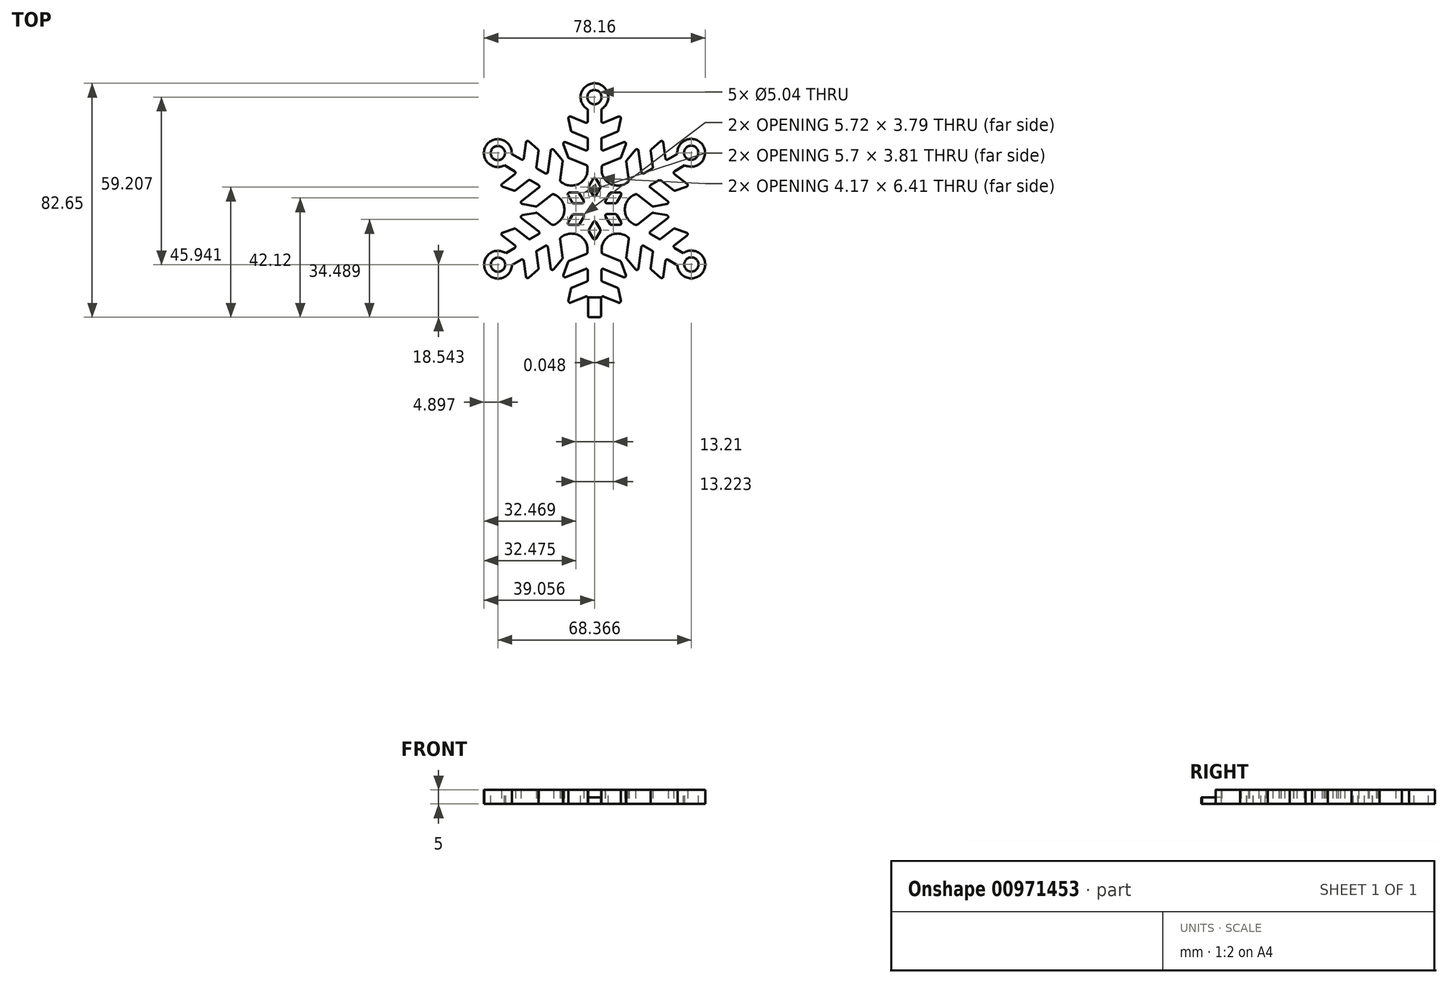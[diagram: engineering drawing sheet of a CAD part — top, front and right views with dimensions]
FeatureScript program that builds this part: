
annotation { "Feature Type Name" : "Feature", "Feature Type Description" : "" }
export const myFeature = defineFeature(function(context is Context, id is Id, definition is map)
    precondition{}
    {
        {
            var Q0;
            Q0=qCreatedBy(makeId("Top.planeOp"),FACE);
            var sketch = newSketch(context, id + "F0", { "sketchPlane" : qUnion([Q0])});
            skCircle(sketch, "E0", {"center": v(-1.7, 0) * mm, "radius": 57.15 * mm});
            skSolve(sketch);
        }
        {
            var Q0;
            Q0=makeQuery(id+"F0.imprint","IMPRINT",FACE,{"disambiguationData":[TD([[makeQuery(id+"F0.imprint","IMPRINT",EDGE,{"derivedFrom":sQuery(id+"F0.wireOp",EDGE,"E0")}),1.0]])]});
            extrude(context, id + "F1", {"entities" : qUnion([Q0]), "offsetDistance" : 25 * mm, "depth" : 6 * mm});
        }
        {
            var Q0;
            Q0=makeQuery(id+"F1.opExtrude","CAP_FACE",FACE,{"disambiguationData":[OSD([sQuery(id+"F0.wireOp",EDGE,"E0")])],"isStart":false});
            var sketch = newSketch(context, id + "F2", { "sketchPlane" : qUnion([Q0])});
            skCircle(sketch, "E1", {"center": v(0, 0) * mm, "radius": 19.2 * mm, "construction": true});
            skLineSegment(sketch, "E2", {"start": v(-23.76, 13.72) * mm, "end": v(23.98, -13.85) * mm, "construction": true});
            skLineSegment(sketch, "E3", {"start": v(-14.54, -25.2) * mm, "end": v(14.87, 25.76) * mm, "construction": true});
            skLineSegment(sketch, "E4", {"start": v(-12.51, -6.43) * mm, "end": v(-10.56, -3.05) * mm});
            skLineSegment(sketch, "E5", {"start": v(-9.89, -2.65) * mm, "end": v(-5.8, -2.57) * mm});
            skLineSegment(sketch, "E6", {"start": v(-5.1, -3.76) * mm, "end": v(-7.1, -7.22) * mm});
            skLineSegment(sketch, "E7", {"start": v(-7.8, -7.62) * mm, "end": v(-11.82, -7.62) * mm});
            skLineSegment(sketch, "E8", {"start": v(-13.2, -7.62) * mm, "end": v(-4.4, -2.54) * mm, "construction": true});
            skLineSegment(sketch, "E9", {"start": v(-10.33, -2.66) * mm, "end": v(-7.33, -7.62) * mm, "construction": true});
            skLineSegment(sketch, "E10", {"start": v(0, 0) * mm, "end": v(-16.62, -9.6) * mm, "construction": true});
            skPoint(sketch, "E11.visualSharp", {"position": v(-10.33, -2.66) * mm});
            skArc(sketch, "E11.filletArc", {"start": v(-9.89, -2.65) * mm, "mid": v(-10.27, -2.76) * mm, "end": v(-10.56, -3.05) * mm});
            skPoint(sketch, "E12.visualSharp", {"position": v(-7.33, -7.62) * mm});
            skArc(sketch, "E12.filletArc", {"start": v(-7.8, -7.62) * mm, "mid": v(-7.4, -7.51) * mm, "end": v(-7.1, -7.22) * mm});
            skPoint(sketch, "E13.visualSharp", {"position": v(-4.4, -2.54) * mm});
            skArc(sketch, "E13.filletArc", {"start": v(-5.1, -3.76) * mm, "mid": v(-5.1, -2.96) * mm, "end": v(-5.8, -2.57) * mm});
            skPoint(sketch, "E14.visualSharp", {"position": v(-13.2, -7.62) * mm});
            skArc(sketch, "E14.filletArc", {"start": v(-12.51, -6.43) * mm, "mid": v(-12.51, -7.22) * mm, "end": v(-11.82, -7.62) * mm});
            skArc(sketch, "E15.1.0", {"start": v(-0.69, -14.05) * mm, "mid": v(0, -14.45) * mm, "end": v(0.69, -14.05) * mm});
            skLineSegment(sketch, "E15.1.1", {"start": v(2.7, -10.56) * mm, "end": v(0.69, -14.05) * mm});
            skArc(sketch, "E15.1.2", {"start": v(2.7, -10.56) * mm, "mid": v(2.81, -10.16) * mm, "end": v(2.7, -9.76) * mm});
            skLineSegment(sketch, "E15.1.3", {"start": v(0.7, -6.3) * mm, "end": v(2.7, -9.76) * mm});
            skArc(sketch, "E15.1.4", {"start": v(0.7, -6.3) * mm, "mid": v(0, -5.9) * mm, "end": v(-0.68, -6.31) * mm});
            skLineSegment(sketch, "E15.1.5", {"start": v(-2.65, -9.89) * mm, "end": v(-0.68, -6.31) * mm});
            skArc(sketch, "E15.1.6", {"start": v(-2.65, -9.89) * mm, "mid": v(-2.75, -10.28) * mm, "end": v(-2.64, -10.67) * mm});
            skLineSegment(sketch, "E15.1.7", {"start": v(-0.69, -14.05) * mm, "end": v(-2.64, -10.67) * mm});
            skArc(sketch, "E15.2.0", {"start": v(11.82, -7.62) * mm, "mid": v(12.51, -7.22) * mm, "end": v(12.51, -6.43) * mm});
            skLineSegment(sketch, "E15.2.1", {"start": v(10.5, -2.94) * mm, "end": v(12.51, -6.43) * mm});
            skArc(sketch, "E15.2.2", {"start": v(10.5, -2.94) * mm, "mid": v(10.2, -2.65) * mm, "end": v(9.8, -2.54) * mm});
            skLineSegment(sketch, "E15.2.3", {"start": v(5.8, -2.54) * mm, "end": v(9.8, -2.54) * mm});
            skArc(sketch, "E15.2.4", {"start": v(5.8, -2.54) * mm, "mid": v(5.12, -2.94) * mm, "end": v(5.13, -3.74) * mm});
            skLineSegment(sketch, "E15.2.5", {"start": v(7.24, -7.24) * mm, "end": v(5.13, -3.74) * mm});
            skArc(sketch, "E15.2.6", {"start": v(7.24, -7.24) * mm, "mid": v(7.53, -7.52) * mm, "end": v(7.92, -7.62) * mm});
            skLineSegment(sketch, "E15.2.7", {"start": v(11.82, -7.62) * mm, "end": v(7.92, -7.62) * mm});
            skArc(sketch, "E15.3.0", {"start": v(12.51, 6.43) * mm, "mid": v(12.51, 7.22) * mm, "end": v(11.82, 7.62) * mm});
            skLineSegment(sketch, "E15.3.1", {"start": v(7.8, 7.62) * mm, "end": v(11.82, 7.62) * mm});
            skArc(sketch, "E15.3.2", {"start": v(7.8, 7.62) * mm, "mid": v(7.4, 7.51) * mm, "end": v(7.1, 7.22) * mm});
            skLineSegment(sketch, "E15.3.3", {"start": v(5.1, 3.76) * mm, "end": v(7.1, 7.22) * mm});
            skArc(sketch, "E15.3.4", {"start": v(5.1, 3.76) * mm, "mid": v(5.1, 2.96) * mm, "end": v(5.8, 2.57) * mm});
            skLineSegment(sketch, "E15.3.5", {"start": v(9.89, 2.65) * mm, "end": v(5.8, 2.57) * mm});
            skArc(sketch, "E15.3.6", {"start": v(9.89, 2.65) * mm, "mid": v(10.27, 2.76) * mm, "end": v(10.56, 3.05) * mm});
            skLineSegment(sketch, "E15.3.7", {"start": v(12.51, 6.43) * mm, "end": v(10.56, 3.05) * mm});
            skArc(sketch, "E15.4.0", {"start": v(0.69, 14.05) * mm, "mid": v(0, 14.45) * mm, "end": v(-0.69, 14.05) * mm});
            skLineSegment(sketch, "E15.4.1", {"start": v(-2.7, 10.56) * mm, "end": v(-0.69, 14.05) * mm});
            skArc(sketch, "E15.4.2", {"start": v(-2.7, 10.56) * mm, "mid": v(-2.81, 10.16) * mm, "end": v(-2.7, 9.76) * mm});
            skLineSegment(sketch, "E15.4.3", {"start": v(-0.7, 6.3) * mm, "end": v(-2.7, 9.76) * mm});
            skArc(sketch, "E15.4.4", {"start": v(-0.7, 6.3) * mm, "mid": v(0, 5.9) * mm, "end": v(0.68, 6.31) * mm});
            skLineSegment(sketch, "E15.4.5", {"start": v(2.65, 9.89) * mm, "end": v(0.68, 6.31) * mm});
            skArc(sketch, "E15.4.6", {"start": v(2.65, 9.89) * mm, "mid": v(2.75, 10.28) * mm, "end": v(2.64, 10.67) * mm});
            skLineSegment(sketch, "E15.4.7", {"start": v(0.69, 14.05) * mm, "end": v(2.64, 10.67) * mm});
            skArc(sketch, "E15.5.0", {"start": v(-11.82, 7.62) * mm, "mid": v(-12.51, 7.22) * mm, "end": v(-12.51, 6.43) * mm});
            skLineSegment(sketch, "E15.5.1", {"start": v(-10.5, 2.94) * mm, "end": v(-12.51, 6.43) * mm});
            skArc(sketch, "E15.5.2", {"start": v(-10.5, 2.94) * mm, "mid": v(-10.2, 2.65) * mm, "end": v(-9.8, 2.54) * mm});
            skLineSegment(sketch, "E15.5.3", {"start": v(-5.8, 2.54) * mm, "end": v(-9.8, 2.54) * mm});
            skArc(sketch, "E15.5.4", {"start": v(-5.8, 2.54) * mm, "mid": v(-5.12, 2.94) * mm, "end": v(-5.13, 3.74) * mm});
            skLineSegment(sketch, "E15.5.5", {"start": v(-7.24, 7.24) * mm, "end": v(-5.13, 3.74) * mm});
            skArc(sketch, "E15.5.6", {"start": v(-7.24, 7.24) * mm, "mid": v(-7.53, 7.52) * mm, "end": v(-7.92, 7.62) * mm});
            skLineSegment(sketch, "E15.5.7", {"start": v(-11.82, 7.62) * mm, "end": v(-7.92, 7.62) * mm});
            skSolve(sketch);
        }
        {
            var Q0;
            Q0=makeQuery(id+"F2.imprint","IMPRINT",FACE,{"disambiguationData":[TD([[makeQuery(id+"F2.imprint","IMPRINT",EDGE,{"derivedFrom":sQuery(id+"F2.wireOp",EDGE,"E15.4.0")}),1.0]])]});
            var Q1;
            Q1=makeQuery(id+"F2.imprint","IMPRINT",FACE,{"disambiguationData":[TD([[makeQuery(id+"F2.imprint","IMPRINT",EDGE,{"derivedFrom":sQuery(id+"F2.wireOp",EDGE,"E15.3.0")}),1.0]])]});
            var Q2;
            Q2=makeQuery(id+"F2.imprint","IMPRINT",FACE,{"disambiguationData":[TD([[makeQuery(id+"F2.imprint","IMPRINT",EDGE,{"derivedFrom":sQuery(id+"F2.wireOp",EDGE,"E15.2.0")}),1.0]])]});
            var Q3;
            Q3=makeQuery(id+"F2.imprint","IMPRINT",FACE,{"disambiguationData":[TD([[makeQuery(id+"F2.imprint","IMPRINT",EDGE,{"derivedFrom":sQuery(id+"F2.wireOp",EDGE,"E15.1.0")}),1.0]])]});
            var Q4;
            Q4=makeQuery(id+"F2.imprint","IMPRINT",FACE,{"disambiguationData":[TD([[makeQuery(id+"F2.imprint","IMPRINT",EDGE,{"derivedFrom":sQuery(id+"F2.wireOp",EDGE,"E4")}),-1.0]])]});
            var Q5;
            Q5=makeQuery(id+"F2.imprint","IMPRINT",FACE,{"disambiguationData":[TD([[makeQuery(id+"F2.imprint","IMPRINT",EDGE,{"derivedFrom":sQuery(id+"F2.wireOp",EDGE,"E15.5.0")}),1.0]])]});
            extrude(context, id + "F3", {"entities" : qUnion([Q0, Q1, Q2, Q3, Q4, Q5]), "operationType" : NewBodyOperationType.REMOVE, "endBound" : BoundingType.UP_TO_NEXT, "oppositeDirection" : true, "depth" : 25.4 * mm});
        }
        {
            var Q0;
            Q0=makeQuery(id+"F1.opExtrude","CAP_FACE",FACE,{"disambiguationData":[OSD([sQuery(id+"F0.wireOp",EDGE,"E0")])],"isStart":true});
            var sketch = newSketch(context, id + "F4", { "sketchPlane" : qUnion([Q0])});
            skLineSegment(sketch, "E16", {"start": v(0, 0) * mm, "end": v(0, -57.12) * mm, "construction": true});
            skLineSegment(sketch, "E17", {"start": v(-50.77, -29.31) * mm, "end": v(48.2, 27.83) * mm, "construction": true});
            skLineSegment(sketch, "E18", {"start": v(48.2, -27.83) * mm, "end": v(-50.77, 29.31) * mm, "construction": true});
            skLineSegment(sketch, "E19", {"start": v(0, 0) * mm, "end": v(-29, -50.22) * mm, "construction": true});
            skLineSegment(sketch, "E20", {"start": v(0, -50.3) * mm, "end": v(-2.38, -50.3) * mm});
            skLineSegment(sketch, "E21", {"start": v(-3.17, -49.5) * mm, "end": v(-3.17, -41.32) * mm});
            skLineSegment(sketch, "E22", {"start": v(-4.27, -40.58) * mm, "end": v(-11.21, -43.43) * mm});
            skLineSegment(sketch, "E23", {"start": v(-12.3, -42.54) * mm, "end": v(-11.2, -36.94) * mm});
            skLineSegment(sketch, "E24", {"start": v(-10.72, -36.36) * mm, "end": v(-3.67, -33.47) * mm});
            skLineSegment(sketch, "E25", {"start": v(-3.18, -32.74) * mm, "end": v(-3.18, -28.3) * mm});
            skLineSegment(sketch, "E26", {"start": v(-4.27, -27.56) * mm, "end": v(-13.67, -31.41) * mm});
            skLineSegment(sketch, "E27", {"start": v(-14.72, -30.41) * mm, "end": v(-12.58, -24.39) * mm});
            skLineSegment(sketch, "E28", {"start": v(-12.14, -23.92) * mm, "end": v(-3.91, -20.55) * mm});
            skPoint(sketch, "E29.endSnap0", {"position": v(0, -28.56) * mm});
            skLineSegment(sketch, "E30", {"start": v(0, 0) * mm, "end": v(-41.26, -41.26) * mm, "construction": true});
            skPoint(sketch, "E31.visualSharp", {"position": v(-3.17, -40.13) * mm});
            skArc(sketch, "E31.filletArc", {"start": v(-3.17, -41.32) * mm, "mid": v(-3.53, -40.66) * mm, "end": v(-4.27, -40.58) * mm});
            skPoint(sketch, "E32.visualSharp", {"position": v(-12.57, -43.99) * mm});
            skArc(sketch, "E32.filletArc", {"start": v(-12.3, -42.54) * mm, "mid": v(-12.02, -43.3) * mm, "end": v(-11.21, -43.43) * mm});
            skPoint(sketch, "E33.visualSharp", {"position": v(-11.11, -36.52) * mm});
            skArc(sketch, "E33.filletArc", {"start": v(-10.72, -36.36) * mm, "mid": v(-11.03, -36.6) * mm, "end": v(-11.2, -36.94) * mm});
            skPoint(sketch, "E34.visualSharp", {"position": v(-3.18, -33.27) * mm});
            skArc(sketch, "E34.filletArc", {"start": v(-3.67, -33.47) * mm, "mid": v(-3.3, -33.18) * mm, "end": v(-3.17, -32.74) * mm});
            skPoint(sketch, "E35.visualSharp", {"position": v(-3.18, -27.1) * mm});
            skArc(sketch, "E35.filletArc", {"start": v(-3.17, -28.3) * mm, "mid": v(-3.53, -27.63) * mm, "end": v(-4.27, -27.56) * mm});
            skPoint(sketch, "E36.visualSharp", {"position": v(-15.31, -32.09) * mm});
            skArc(sketch, "E36.filletArc", {"start": v(-14.72, -30.41) * mm, "mid": v(-14.52, -31.25) * mm, "end": v(-13.67, -31.41) * mm});
            skPoint(sketch, "E37.visualSharp", {"position": v(-12.47, -24.06) * mm});
            skArc(sketch, "E37.filletArc", {"start": v(-12.14, -23.92) * mm, "mid": v(-12.41, -24.1) * mm, "end": v(-12.58, -24.39) * mm});
            skPoint(sketch, "E38.visualSharp", {"position": v(-3.18, -20.24) * mm});
            skArc(sketch, "E38.filletArc", {"start": v(-3.91, -20.55) * mm, "mid": v(-3.57, -20.27) * mm, "end": v(-3.42, -19.86) * mm});
            skPoint(sketch, "E39.visualSharp", {"position": v(-9.43, -13.02) * mm});
            skPoint(sketch, "E40.visualSharp", {"position": v(-19.76, -16.16) * mm});
            skLineSegment(sketch, "E41.MirrorCS", {"start": v(0, -50.3) * mm, "end": v(2.38, -50.3) * mm});
            skLineSegment(sketch, "E42.MirrorCS", {"start": v(3.18, -49.5) * mm, "end": v(3.18, -41.32) * mm});
            skArc(sketch, "E43.MirrorCS", {"start": v(3.17, -41.32) * mm, "mid": v(3.53, -40.66) * mm, "end": v(4.27, -40.58) * mm});
            skLineSegment(sketch, "E44.MirrorCS", {"start": v(4.27, -40.58) * mm, "end": v(11.21, -43.43) * mm});
            skArc(sketch, "E45.MirrorCS", {"start": v(12.3, -42.54) * mm, "mid": v(12.02, -43.3) * mm, "end": v(11.21, -43.43) * mm});
            skLineSegment(sketch, "E46.MirrorCS", {"start": v(12.3, -42.54) * mm, "end": v(11.2, -36.94) * mm});
            skArc(sketch, "E47.MirrorCS", {"start": v(10.72, -36.36) * mm, "mid": v(11.03, -36.6) * mm, "end": v(11.2, -36.94) * mm});
            skLineSegment(sketch, "E48.MirrorCS", {"start": v(10.72, -36.36) * mm, "end": v(3.67, -33.47) * mm});
            skArc(sketch, "E49.MirrorCS", {"start": v(3.67, -33.47) * mm, "mid": v(3.3, -33.18) * mm, "end": v(3.17, -32.74) * mm});
            skLineSegment(sketch, "E50.MirrorCS", {"start": v(3.18, -32.74) * mm, "end": v(3.18, -28.3) * mm});
            skArc(sketch, "E51.MirrorCS", {"start": v(3.17, -28.3) * mm, "mid": v(3.53, -27.63) * mm, "end": v(4.27, -27.56) * mm});
            skLineSegment(sketch, "E52.MirrorCS", {"start": v(4.27, -27.56) * mm, "end": v(13.67, -31.41) * mm});
            skArc(sketch, "E53.MirrorCS", {"start": v(14.72, -30.41) * mm, "mid": v(14.52, -31.25) * mm, "end": v(13.67, -31.41) * mm});
            skLineSegment(sketch, "E54.MirrorCS", {"start": v(14.72, -30.41) * mm, "end": v(12.58, -24.39) * mm});
            skArc(sketch, "E55.MirrorCS", {"start": v(12.14, -23.92) * mm, "mid": v(12.41, -24.1) * mm, "end": v(12.58, -24.39) * mm});
            skLineSegment(sketch, "E56.MirrorCS", {"start": v(12.14, -23.92) * mm, "end": v(3.91, -20.55) * mm});
            skArc(sketch, "E57.MirrorCS", {"start": v(3.91, -20.55) * mm, "mid": v(3.57, -20.27) * mm, "end": v(3.42, -19.86) * mm});
            skPoint(sketch, "E58.visualSharp", {"position": v(-3.17, -50.3) * mm});
            skArc(sketch, "E58.filletArc", {"start": v(-3.17, -49.5) * mm, "mid": v(-2.94, -50.06) * mm, "end": v(-2.38, -50.3) * mm});
            skPoint(sketch, "E59.visualSharp", {"position": v(3.17, -50.3) * mm});
            skArc(sketch, "E59.filletArc", {"start": v(2.38, -50.3) * mm, "mid": v(2.94, -50.06) * mm, "end": v(3.17, -49.5) * mm});
            skLineSegment(sketch, "E60.1.0", {"start": v(43.33, -10.43) * mm, "end": v(37.93, -8.58) * mm});
            skLineSegment(sketch, "E60.1.1", {"start": v(26.47, -27.27) * mm, "end": v(27.5, -19.72) * mm});
            skLineSegment(sketch, "E60.1.2", {"start": v(44.8, -21.8) * mm, "end": v(37.7, -17.71) * mm});
            skPoint(sketch, "E60.1.3", {"position": v(25.07, -14.09) * mm});
            skLineSegment(sketch, "E60.1.4", {"start": v(31.04, -31.72) * mm, "end": v(26.74, -27.97) * mm});
            skLineSegment(sketch, "E60.1.5", {"start": v(14.99, -22.28) * mm, "end": v(16.18, -13.47) * mm});
            skLineSegment(sketch, "E60.1.6", {"start": v(41.62, -27.3) * mm, "end": v(34.53, -23.21) * mm});
            skLineSegment(sketch, "E60.1.7", {"start": v(22.07, -17.28) * mm, "end": v(20.7, -27.35) * mm});
            skPoint(sketch, "E60.1.8", {"position": v(16.28, -12.68) * mm});
            skPoint(sketch, "E60.1.9", {"position": v(32.15, -32.69) * mm});
            skPoint(sketch, "E60.1.10", {"position": v(45.48, -22.2) * mm});
            skLineSegment(sketch, "E60.1.11", {"start": v(37.19, -8.7) * mm, "end": v(31.16, -13.36) * mm});
            skPoint(sketch, "E60.1.12", {"position": v(26.41, -27.7) * mm});
            skLineSegment(sketch, "E60.1.13", {"start": v(30.28, -13.42) * mm, "end": v(26.43, -11.2) * mm});
            skPoint(sketch, "E60.1.14", {"position": v(22.23, -16.1) * mm});
            skLineSegment(sketch, "E60.1.15", {"start": v(26.34, -9.88) * mm, "end": v(34.38, -3.67) * mm});
            skLineSegment(sketch, "E60.1.16", {"start": v(34.04, -2.26) * mm, "end": v(27.75, -1.1) * mm});
            skPoint(sketch, "E60.1.17", {"position": v(20.47, -29.1) * mm});
            skLineSegment(sketch, "E60.1.18", {"start": v(27.12, -1.25) * mm, "end": v(20.09, -6.69) * mm});
            skPoint(sketch, "E60.1.19", {"position": v(14.94, -22.63) * mm});
            skPoint(sketch, "E60.1.20", {"position": v(33.5, -22.62) * mm});
            skLineSegment(sketch, "E60.1.21", {"start": v(37.62, -16.4) * mm, "end": v(43.55, -11.8) * mm});
            skLineSegment(sketch, "E60.1.22", {"start": v(33.35, -23.8) * mm, "end": v(32.34, -31.23) * mm});
            skLineSegment(sketch, "E60.1.23", {"start": v(27.1, -18.92) * mm, "end": v(23.25, -16.7) * mm});
            skPoint(sketch, "E60.1.24", {"position": v(42.3, -27.7) * mm});
            skLineSegment(sketch, "E60.1.25", {"start": v(19.32, -27.76) * mm, "end": v(15.17, -22.9) * mm});
            skPoint(sketch, "E60.1.26", {"position": v(27.56, -19.19) * mm});
            skArc(sketch, "E60.1.27", {"start": v(43.33, -10.43) * mm, "mid": v(43.85, -11.05) * mm, "end": v(43.55, -11.8) * mm});
            skArc(sketch, "E60.1.28", {"start": v(37.19, -8.7) * mm, "mid": v(37.54, -8.55) * mm, "end": v(37.93, -8.58) * mm});
            skArc(sketch, "E60.1.29", {"start": v(31.16, -13.36) * mm, "mid": v(30.73, -13.53) * mm, "end": v(30.28, -13.42) * mm});
            skArc(sketch, "E60.1.30", {"start": v(19.32, -27.76) * mm, "mid": v(20.15, -28) * mm, "end": v(20.7, -27.35) * mm});
            skArc(sketch, "E60.1.31", {"start": v(34.04, -2.26) * mm, "mid": v(34.66, -2.86) * mm, "end": v(34.38, -3.67) * mm});
            skArc(sketch, "E60.1.32", {"start": v(27.12, -1.25) * mm, "mid": v(27.42, -1.1) * mm, "end": v(27.75, -1.1) * mm});
            skArc(sketch, "E60.1.33", {"start": v(20.09, -6.69) * mm, "mid": v(19.68, -6.85) * mm, "end": v(19.25, -6.77) * mm});
            skArc(sketch, "E60.1.34", {"start": v(37.7, -17.71) * mm, "mid": v(37.31, -17.08) * mm, "end": v(37.62, -16.4) * mm});
            skLineSegment(sketch, "E60.1.35", {"start": v(43.9, -24.95) * mm, "end": v(42.7, -27.01) * mm});
            skArc(sketch, "E60.1.36", {"start": v(31.04, -31.72) * mm, "mid": v(31.84, -31.86) * mm, "end": v(32.34, -31.23) * mm});
            skArc(sketch, "E60.1.37", {"start": v(34.53, -23.21) * mm, "mid": v(33.78, -23.19) * mm, "end": v(33.35, -23.8) * mm});
            skArc(sketch, "E60.1.38", {"start": v(26.47, -27.27) * mm, "mid": v(26.51, -27.65) * mm, "end": v(26.74, -27.97) * mm});
            skArc(sketch, "E60.1.39", {"start": v(23.25, -16.7) * mm, "mid": v(22.5, -16.67) * mm, "end": v(22.07, -17.28) * mm});
            skArc(sketch, "E60.1.40", {"start": v(45.08, -22.89) * mm, "mid": v(45.16, -22.29) * mm, "end": v(44.8, -21.8) * mm});
            skArc(sketch, "E60.1.41", {"start": v(26.43, -11.2) * mm, "mid": v(26.03, -10.57) * mm, "end": v(26.34, -9.88) * mm});
            skArc(sketch, "E60.1.42", {"start": v(14.99, -22.28) * mm, "mid": v(15.01, -22.6) * mm, "end": v(15.17, -22.9) * mm});
            skArc(sketch, "E60.1.43", {"start": v(16.18, -13.47) * mm, "mid": v(16.11, -13.03) * mm, "end": v(15.83, -12.7) * mm});
            skLineSegment(sketch, "E60.1.44", {"start": v(43.9, -24.95) * mm, "end": v(45.08, -22.89) * mm});
            skArc(sketch, "E60.1.45", {"start": v(27.5, -19.72) * mm, "mid": v(27.42, -19.26) * mm, "end": v(27.1, -18.92) * mm});
            skArc(sketch, "E60.1.46", {"start": v(41.62, -27.3) * mm, "mid": v(42.22, -27.38) * mm, "end": v(42.7, -27.01) * mm});
            skLineSegment(sketch, "E60.2.0", {"start": v(31.04, 32.5) * mm, "end": v(26.74, 28.75) * mm});
            skLineSegment(sketch, "E60.2.1", {"start": v(37.19, 9.49) * mm, "end": v(31.16, 14.15) * mm});
            skLineSegment(sketch, "E60.2.2", {"start": v(41.62, 28.09) * mm, "end": v(34.53, 24) * mm});
            skPoint(sketch, "E60.2.3", {"position": v(25.07, 14.87) * mm});
            skLineSegment(sketch, "E60.2.4", {"start": v(43.33, 11.21) * mm, "end": v(37.93, 9.36) * mm});
            skLineSegment(sketch, "E60.2.5", {"start": v(27.12, 2.04) * mm, "end": v(20.09, 7.47) * mm});
            skLineSegment(sketch, "E60.2.6", {"start": v(44.8, 22.59) * mm, "end": v(37.7, 18.5) * mm});
            skLineSegment(sketch, "E60.2.7", {"start": v(26.34, 10.67) * mm, "end": v(34.38, 4.45) * mm});
            skPoint(sketch, "E60.2.8", {"position": v(19.46, 7.96) * mm});
            skPoint(sketch, "E60.2.9", {"position": v(44.72, 11.7) * mm});
            skPoint(sketch, "E60.2.10", {"position": v(42.3, 28.48) * mm});
            skLineSegment(sketch, "E60.2.11", {"start": v(26.47, 28.05) * mm, "end": v(27.5, 20.5) * mm});
            skPoint(sketch, "E60.2.12", {"position": v(37.53, 9.23) * mm});
            skLineSegment(sketch, "E60.2.13", {"start": v(27.1, 19.7) * mm, "end": v(23.25, 17.48) * mm});
            skPoint(sketch, "E60.2.14", {"position": v(25.4, 11.4) * mm});
            skLineSegment(sketch, "E60.2.15", {"start": v(22.07, 18.06) * mm, "end": v(20.7, 28.13) * mm});
            skLineSegment(sketch, "E60.2.16", {"start": v(19.32, 28.54) * mm, "end": v(15.17, 23.68) * mm});
            skPoint(sketch, "E60.2.17", {"position": v(35.78, 3.37) * mm});
            skLineSegment(sketch, "E60.2.18", {"start": v(14.99, 23.06) * mm, "end": v(16.18, 14.25) * mm});
            skPoint(sketch, "E60.2.19", {"position": v(27.4, 1.82) * mm});
            skPoint(sketch, "E60.2.20", {"position": v(36.68, 17.9) * mm});
            skLineSegment(sketch, "E60.2.21", {"start": v(33.35, 24.58) * mm, "end": v(32.34, 32.01) * mm});
            skLineSegment(sketch, "E60.2.22", {"start": v(37.62, 17.18) * mm, "end": v(43.55, 12.6) * mm});
            skLineSegment(sketch, "E60.2.23", {"start": v(30.28, 14.2) * mm, "end": v(26.43, 11.98) * mm});
            skPoint(sketch, "E60.2.24", {"position": v(45.48, 22.98) * mm});
            skLineSegment(sketch, "E60.2.25", {"start": v(34.04, 3.05) * mm, "end": v(27.75, 1.88) * mm});
            skPoint(sketch, "E60.2.26", {"position": v(30.74, 14.47) * mm});
            skArc(sketch, "E60.2.27", {"start": v(31.04, 32.5) * mm, "mid": v(31.84, 32.65) * mm, "end": v(32.34, 32.01) * mm});
            skArc(sketch, "E60.2.28", {"start": v(26.47, 28.05) * mm, "mid": v(26.51, 28.44) * mm, "end": v(26.74, 28.75) * mm});
            skArc(sketch, "E60.2.29", {"start": v(27.5, 20.5) * mm, "mid": v(27.42, 20.04) * mm, "end": v(27.1, 19.7) * mm});
            skArc(sketch, "E60.2.30", {"start": v(34.04, 3.05) * mm, "mid": v(34.66, 3.64) * mm, "end": v(34.38, 4.45) * mm});
            skArc(sketch, "E60.2.31", {"start": v(19.32, 28.54) * mm, "mid": v(20.15, 28.79) * mm, "end": v(20.7, 28.13) * mm});
            skArc(sketch, "E60.2.32", {"start": v(14.99, 23.06) * mm, "mid": v(15.01, 23.39) * mm, "end": v(15.17, 23.68) * mm});
            skArc(sketch, "E60.2.33", {"start": v(16.18, 14.25) * mm, "mid": v(16.11, 13.81) * mm, "end": v(15.83, 13.48) * mm});
            skArc(sketch, "E60.2.34", {"start": v(34.53, 24) * mm, "mid": v(33.78, 23.97) * mm, "end": v(33.35, 24.58) * mm});
            skLineSegment(sketch, "E60.2.35", {"start": v(43.9, 25.73) * mm, "end": v(45.08, 23.67) * mm});
            skArc(sketch, "E60.2.36", {"start": v(43.33, 11.21) * mm, "mid": v(43.85, 11.83) * mm, "end": v(43.55, 12.6) * mm});
            skArc(sketch, "E60.2.37", {"start": v(37.7, 18.5) * mm, "mid": v(37.31, 17.86) * mm, "end": v(37.62, 17.18) * mm});
            skArc(sketch, "E60.2.38", {"start": v(37.19, 9.49) * mm, "mid": v(37.54, 9.33) * mm, "end": v(37.93, 9.36) * mm});
            skArc(sketch, "E60.2.39", {"start": v(26.43, 11.98) * mm, "mid": v(26.03, 11.35) * mm, "end": v(26.34, 10.67) * mm});
            skArc(sketch, "E60.2.40", {"start": v(42.7, 27.8) * mm, "mid": v(42.22, 28.16) * mm, "end": v(41.62, 28.09) * mm});
            skArc(sketch, "E60.2.41", {"start": v(23.25, 17.48) * mm, "mid": v(22.5, 17.46) * mm, "end": v(22.07, 18.06) * mm});
            skArc(sketch, "E60.2.42", {"start": v(27.12, 2.04) * mm, "mid": v(27.42, 1.9) * mm, "end": v(27.75, 1.88) * mm});
            skArc(sketch, "E60.2.43", {"start": v(20.09, 7.47) * mm, "mid": v(19.68, 7.63) * mm, "end": v(19.25, 7.55) * mm});
            skLineSegment(sketch, "E60.2.44", {"start": v(43.9, 25.73) * mm, "end": v(42.7, 27.8) * mm});
            skArc(sketch, "E60.2.45", {"start": v(31.16, 14.15) * mm, "mid": v(30.73, 14.3) * mm, "end": v(30.28, 14.2) * mm});
            skArc(sketch, "E60.2.46", {"start": v(44.8, 22.59) * mm, "mid": v(45.16, 23.07) * mm, "end": v(45.08, 23.67) * mm});
            skLineSegment(sketch, "E60.3.0", {"start": v(-12.3, 43.32) * mm, "end": v(-11.2, 37.73) * mm});
            skLineSegment(sketch, "E60.3.1", {"start": v(10.72, 37.14) * mm, "end": v(3.67, 34.25) * mm});
            skLineSegment(sketch, "E60.3.2", {"start": v(-3.17, 50.28) * mm, "end": v(-3.17, 42.1) * mm});
            skPoint(sketch, "E60.3.3", {"position": v(0, 29.34) * mm});
            skLineSegment(sketch, "E60.3.4", {"start": v(12.3, 43.32) * mm, "end": v(11.2, 37.73) * mm});
            skLineSegment(sketch, "E60.3.5", {"start": v(12.14, 24.7) * mm, "end": v(3.91, 21.33) * mm});
            skLineSegment(sketch, "E60.3.6", {"start": v(3.18, 50.28) * mm, "end": v(3.18, 42.1) * mm});
            skLineSegment(sketch, "E60.3.7", {"start": v(4.27, 28.34) * mm, "end": v(13.67, 32.2) * mm});
            skPoint(sketch, "E60.3.8", {"position": v(3.18, 21.03) * mm});
            skPoint(sketch, "E60.3.9", {"position": v(12.57, 44.77) * mm});
            skPoint(sketch, "E60.3.10", {"position": v(-3.17, 51.07) * mm});
            skLineSegment(sketch, "E60.3.11", {"start": v(-10.72, 37.14) * mm, "end": v(-3.67, 34.25) * mm});
            skPoint(sketch, "E60.3.12", {"position": v(11.11, 37.3) * mm});
            skLineSegment(sketch, "E60.3.13", {"start": v(-3.17, 33.52) * mm, "end": v(-3.17, 29.07) * mm});
            skPoint(sketch, "E60.3.14", {"position": v(3.18, 27.9) * mm});
            skLineSegment(sketch, "E60.3.15", {"start": v(-4.27, 28.34) * mm, "end": v(-13.67, 32.2) * mm});
            skLineSegment(sketch, "E60.3.16", {"start": v(-14.72, 31.2) * mm, "end": v(-12.58, 25.17) * mm});
            skPoint(sketch, "E60.3.17", {"position": v(15.31, 32.87) * mm});
            skLineSegment(sketch, "E60.3.18", {"start": v(-12.14, 24.7) * mm, "end": v(-3.91, 21.33) * mm});
            skPoint(sketch, "E60.3.19", {"position": v(12.47, 24.84) * mm});
            skPoint(sketch, "E60.3.20", {"position": v(3.18, 40.91) * mm});
            skLineSegment(sketch, "E60.3.21", {"start": v(-4.27, 41.36) * mm, "end": v(-11.21, 44.21) * mm});
            skLineSegment(sketch, "E60.3.22", {"start": v(4.27, 41.36) * mm, "end": v(11.21, 44.21) * mm});
            skLineSegment(sketch, "E60.3.23", {"start": v(3.18, 33.52) * mm, "end": v(3.18, 29.07) * mm});
            skPoint(sketch, "E60.3.24", {"position": v(3.18, 51.07) * mm});
            skLineSegment(sketch, "E60.3.25", {"start": v(14.72, 31.2) * mm, "end": v(12.58, 25.17) * mm});
            skPoint(sketch, "E60.3.26", {"position": v(3.18, 34.05) * mm});
            skArc(sketch, "E60.3.27", {"start": v(-12.3, 43.32) * mm, "mid": v(-12.02, 44.1) * mm, "end": v(-11.21, 44.21) * mm});
            skArc(sketch, "E60.3.28", {"start": v(-10.72, 37.14) * mm, "mid": v(-11.03, 37.38) * mm, "end": v(-11.2, 37.73) * mm});
            skArc(sketch, "E60.3.29", {"start": v(-3.67, 34.25) * mm, "mid": v(-3.3, 33.96) * mm, "end": v(-3.17, 33.52) * mm});
            skArc(sketch, "E60.3.30", {"start": v(14.72, 31.2) * mm, "mid": v(14.52, 32.04) * mm, "end": v(13.67, 32.2) * mm});
            skArc(sketch, "E60.3.31", {"start": v(-14.72, 31.2) * mm, "mid": v(-14.52, 32.04) * mm, "end": v(-13.67, 32.2) * mm});
            skArc(sketch, "E60.3.32", {"start": v(-12.14, 24.7) * mm, "mid": v(-12.41, 24.89) * mm, "end": v(-12.58, 25.17) * mm});
            skArc(sketch, "E60.3.33", {"start": v(-3.91, 21.33) * mm, "mid": v(-3.57, 21.06) * mm, "end": v(-3.42, 20.64) * mm});
            skArc(sketch, "E60.3.34", {"start": v(-3.17, 42.1) * mm, "mid": v(-3.53, 41.44) * mm, "end": v(-4.27, 41.36) * mm});
            skLineSegment(sketch, "E60.3.35", {"start": v(0, 51.07) * mm, "end": v(2.38, 51.07) * mm});
            skArc(sketch, "E60.3.36", {"start": v(12.3, 43.32) * mm, "mid": v(12.02, 44.1) * mm, "end": v(11.21, 44.21) * mm});
            skArc(sketch, "E60.3.37", {"start": v(3.18, 42.1) * mm, "mid": v(3.53, 41.44) * mm, "end": v(4.27, 41.36) * mm});
            skArc(sketch, "E60.3.38", {"start": v(10.72, 37.14) * mm, "mid": v(11.03, 37.38) * mm, "end": v(11.2, 37.73) * mm});
            skArc(sketch, "E60.3.39", {"start": v(3.18, 29.07) * mm, "mid": v(3.53, 28.41) * mm, "end": v(4.27, 28.34) * mm});
            skArc(sketch, "E60.3.40", {"start": v(-2.38, 51.07) * mm, "mid": v(-2.94, 50.84) * mm, "end": v(-3.17, 50.28) * mm});
            skArc(sketch, "E60.3.41", {"start": v(-3.17, 29.07) * mm, "mid": v(-3.53, 28.41) * mm, "end": v(-4.27, 28.34) * mm});
            skArc(sketch, "E60.3.42", {"start": v(12.14, 24.7) * mm, "mid": v(12.41, 24.89) * mm, "end": v(12.58, 25.17) * mm});
            skArc(sketch, "E60.3.43", {"start": v(3.91, 21.33) * mm, "mid": v(3.57, 21.06) * mm, "end": v(3.42, 20.64) * mm});
            skLineSegment(sketch, "E60.3.44", {"start": v(0, 51.07) * mm, "end": v(-2.38, 51.07) * mm});
            skArc(sketch, "E60.3.45", {"start": v(3.67, 34.25) * mm, "mid": v(3.3, 33.96) * mm, "end": v(3.18, 33.52) * mm});
            skArc(sketch, "E60.3.46", {"start": v(3.18, 50.28) * mm, "mid": v(2.94, 50.84) * mm, "end": v(2.38, 51.07) * mm});
            skLineSegment(sketch, "E60.4.0", {"start": v(-43.33, 11.21) * mm, "end": v(-37.93, 9.36) * mm});
            skLineSegment(sketch, "E60.4.1", {"start": v(-26.47, 28.05) * mm, "end": v(-27.5, 20.5) * mm});
            skLineSegment(sketch, "E60.4.2", {"start": v(-44.8, 22.59) * mm, "end": v(-37.7, 18.5) * mm});
            skPoint(sketch, "E60.4.3", {"position": v(-25.07, 14.87) * mm});
            skLineSegment(sketch, "E60.4.4", {"start": v(-31.04, 32.5) * mm, "end": v(-26.74, 28.75) * mm});
            skLineSegment(sketch, "E60.4.5", {"start": v(-14.99, 23.06) * mm, "end": v(-16.18, 14.25) * mm});
            skLineSegment(sketch, "E60.4.6", {"start": v(-41.62, 28.09) * mm, "end": v(-34.53, 24) * mm});
            skLineSegment(sketch, "E60.4.7", {"start": v(-22.07, 18.06) * mm, "end": v(-20.7, 28.13) * mm});
            skPoint(sketch, "E60.4.8", {"position": v(-16.28, 13.46) * mm});
            skPoint(sketch, "E60.4.9", {"position": v(-32.15, 33.47) * mm});
            skPoint(sketch, "E60.4.10", {"position": v(-45.48, 22.98) * mm});
            skLineSegment(sketch, "E60.4.11", {"start": v(-37.19, 9.49) * mm, "end": v(-31.16, 14.15) * mm});
            skPoint(sketch, "E60.4.12", {"position": v(-26.41, 28.47) * mm});
            skLineSegment(sketch, "E60.4.13", {"start": v(-30.28, 14.2) * mm, "end": v(-26.43, 11.98) * mm});
            skPoint(sketch, "E60.4.14", {"position": v(-22.23, 16.9) * mm});
            skLineSegment(sketch, "E60.4.15", {"start": v(-26.34, 10.67) * mm, "end": v(-34.38, 4.45) * mm});
            skLineSegment(sketch, "E60.4.16", {"start": v(-34.04, 3.05) * mm, "end": v(-27.75, 1.88) * mm});
            skPoint(sketch, "E60.4.17", {"position": v(-20.47, 29.9) * mm});
            skLineSegment(sketch, "E60.4.18", {"start": v(-27.12, 2.04) * mm, "end": v(-20.09, 7.47) * mm});
            skPoint(sketch, "E60.4.19", {"position": v(-14.94, 23.41) * mm});
            skPoint(sketch, "E60.4.20", {"position": v(-33.5, 23.4) * mm});
            skLineSegment(sketch, "E60.4.21", {"start": v(-37.62, 17.18) * mm, "end": v(-43.55, 12.6) * mm});
            skLineSegment(sketch, "E60.4.22", {"start": v(-33.35, 24.58) * mm, "end": v(-32.34, 32.01) * mm});
            skLineSegment(sketch, "E60.4.23", {"start": v(-27.1, 19.7) * mm, "end": v(-23.25, 17.48) * mm});
            skPoint(sketch, "E60.4.24", {"position": v(-42.3, 28.48) * mm});
            skLineSegment(sketch, "E60.4.25", {"start": v(-19.32, 28.54) * mm, "end": v(-15.17, 23.68) * mm});
            skPoint(sketch, "E60.4.26", {"position": v(-27.56, 19.97) * mm});
            skArc(sketch, "E60.4.27", {"start": v(-43.33, 11.21) * mm, "mid": v(-43.85, 11.83) * mm, "end": v(-43.55, 12.6) * mm});
            skArc(sketch, "E60.4.28", {"start": v(-37.19, 9.49) * mm, "mid": v(-37.54, 9.33) * mm, "end": v(-37.93, 9.36) * mm});
            skArc(sketch, "E60.4.29", {"start": v(-31.16, 14.15) * mm, "mid": v(-30.73, 14.3) * mm, "end": v(-30.28, 14.2) * mm});
            skArc(sketch, "E60.4.30", {"start": v(-19.32, 28.54) * mm, "mid": v(-20.15, 28.79) * mm, "end": v(-20.7, 28.13) * mm});
            skArc(sketch, "E60.4.31", {"start": v(-34.04, 3.05) * mm, "mid": v(-34.66, 3.64) * mm, "end": v(-34.38, 4.45) * mm});
            skArc(sketch, "E60.4.32", {"start": v(-27.12, 2.04) * mm, "mid": v(-27.42, 1.9) * mm, "end": v(-27.75, 1.88) * mm});
            skArc(sketch, "E60.4.33", {"start": v(-20.09, 7.47) * mm, "mid": v(-19.68, 7.63) * mm, "end": v(-19.25, 7.55) * mm});
            skArc(sketch, "E60.4.34", {"start": v(-37.7, 18.5) * mm, "mid": v(-37.31, 17.86) * mm, "end": v(-37.62, 17.18) * mm});
            skLineSegment(sketch, "E60.4.35", {"start": v(-43.9, 25.73) * mm, "end": v(-42.7, 27.8) * mm});
            skArc(sketch, "E60.4.36", {"start": v(-31.04, 32.5) * mm, "mid": v(-31.84, 32.65) * mm, "end": v(-32.34, 32.01) * mm});
            skArc(sketch, "E60.4.37", {"start": v(-34.53, 24) * mm, "mid": v(-33.78, 23.97) * mm, "end": v(-33.35, 24.58) * mm});
            skArc(sketch, "E60.4.38", {"start": v(-26.47, 28.05) * mm, "mid": v(-26.51, 28.44) * mm, "end": v(-26.74, 28.75) * mm});
            skArc(sketch, "E60.4.39", {"start": v(-23.25, 17.48) * mm, "mid": v(-22.5, 17.46) * mm, "end": v(-22.07, 18.06) * mm});
            skArc(sketch, "E60.4.40", {"start": v(-45.08, 23.67) * mm, "mid": v(-45.16, 23.07) * mm, "end": v(-44.8, 22.59) * mm});
            skArc(sketch, "E60.4.41", {"start": v(-26.43, 11.98) * mm, "mid": v(-26.03, 11.35) * mm, "end": v(-26.34, 10.67) * mm});
            skArc(sketch, "E60.4.42", {"start": v(-14.99, 23.06) * mm, "mid": v(-15.01, 23.39) * mm, "end": v(-15.17, 23.68) * mm});
            skArc(sketch, "E60.4.43", {"start": v(-16.18, 14.25) * mm, "mid": v(-16.11, 13.81) * mm, "end": v(-15.83, 13.48) * mm});
            skLineSegment(sketch, "E60.4.44", {"start": v(-43.9, 25.73) * mm, "end": v(-45.08, 23.67) * mm});
            skArc(sketch, "E60.4.45", {"start": v(-27.5, 20.5) * mm, "mid": v(-27.42, 20.04) * mm, "end": v(-27.1, 19.7) * mm});
            skArc(sketch, "E60.4.46", {"start": v(-41.62, 28.09) * mm, "mid": v(-42.22, 28.16) * mm, "end": v(-42.7, 27.8) * mm});
            skLineSegment(sketch, "E60.5.0", {"start": v(-31.04, -31.72) * mm, "end": v(-26.74, -27.97) * mm});
            skLineSegment(sketch, "E60.5.1", {"start": v(-37.19, -8.7) * mm, "end": v(-31.16, -13.36) * mm});
            skLineSegment(sketch, "E60.5.2", {"start": v(-41.62, -27.3) * mm, "end": v(-34.53, -23.21) * mm});
            skPoint(sketch, "E60.5.3", {"position": v(-25.07, -14.09) * mm});
            skLineSegment(sketch, "E60.5.4", {"start": v(-43.33, -10.43) * mm, "end": v(-37.93, -8.58) * mm});
            skLineSegment(sketch, "E60.5.5", {"start": v(-27.12, -1.25) * mm, "end": v(-20.09, -6.69) * mm});
            skLineSegment(sketch, "E60.5.6", {"start": v(-44.8, -21.8) * mm, "end": v(-37.7, -17.71) * mm});
            skLineSegment(sketch, "E60.5.7", {"start": v(-26.34, -9.88) * mm, "end": v(-34.38, -3.67) * mm});
            skPoint(sketch, "E60.5.8", {"position": v(-19.46, -7.18) * mm});
            skPoint(sketch, "E60.5.9", {"position": v(-44.72, -10.9) * mm});
            skPoint(sketch, "E60.5.10", {"position": v(-42.3, -27.7) * mm});
            skLineSegment(sketch, "E60.5.11", {"start": v(-26.47, -27.27) * mm, "end": v(-27.5, -19.72) * mm});
            skPoint(sketch, "E60.5.12", {"position": v(-37.53, -8.44) * mm});
            skLineSegment(sketch, "E60.5.13", {"start": v(-27.1, -18.92) * mm, "end": v(-23.25, -16.7) * mm});
            skPoint(sketch, "E60.5.14", {"position": v(-25.4, -10.6) * mm});
            skLineSegment(sketch, "E60.5.15", {"start": v(-22.07, -17.28) * mm, "end": v(-20.7, -27.35) * mm});
            skLineSegment(sketch, "E60.5.16", {"start": v(-19.32, -27.76) * mm, "end": v(-15.17, -22.9) * mm});
            skPoint(sketch, "E60.5.17", {"position": v(-35.78, -2.59) * mm});
            skLineSegment(sketch, "E60.5.18", {"start": v(-14.99, -22.28) * mm, "end": v(-16.18, -13.47) * mm});
            skPoint(sketch, "E60.5.19", {"position": v(-27.4, -1.04) * mm});
            skPoint(sketch, "E60.5.20", {"position": v(-36.68, -17.12) * mm});
            skLineSegment(sketch, "E60.5.21", {"start": v(-33.35, -23.8) * mm, "end": v(-32.34, -31.23) * mm});
            skLineSegment(sketch, "E60.5.22", {"start": v(-37.62, -16.4) * mm, "end": v(-43.55, -11.8) * mm});
            skLineSegment(sketch, "E60.5.23", {"start": v(-30.28, -13.42) * mm, "end": v(-26.43, -11.2) * mm});
            skPoint(sketch, "E60.5.24", {"position": v(-45.48, -22.2) * mm});
            skLineSegment(sketch, "E60.5.25", {"start": v(-34.04, -2.26) * mm, "end": v(-27.75, -1.1) * mm});
            skPoint(sketch, "E60.5.26", {"position": v(-30.74, -13.69) * mm});
            skArc(sketch, "E60.5.27", {"start": v(-31.04, -31.72) * mm, "mid": v(-31.84, -31.86) * mm, "end": v(-32.34, -31.23) * mm});
            skArc(sketch, "E60.5.28", {"start": v(-26.47, -27.27) * mm, "mid": v(-26.51, -27.65) * mm, "end": v(-26.74, -27.97) * mm});
            skArc(sketch, "E60.5.29", {"start": v(-27.5, -19.72) * mm, "mid": v(-27.42, -19.26) * mm, "end": v(-27.1, -18.92) * mm});
            skArc(sketch, "E60.5.30", {"start": v(-34.04, -2.26) * mm, "mid": v(-34.66, -2.86) * mm, "end": v(-34.38, -3.67) * mm});
            skArc(sketch, "E60.5.31", {"start": v(-19.32, -27.76) * mm, "mid": v(-20.15, -28) * mm, "end": v(-20.7, -27.35) * mm});
            skArc(sketch, "E60.5.32", {"start": v(-14.99, -22.28) * mm, "mid": v(-15.01, -22.6) * mm, "end": v(-15.17, -22.9) * mm});
            skArc(sketch, "E60.5.33", {"start": v(-16.18, -13.47) * mm, "mid": v(-16.11, -13.03) * mm, "end": v(-15.83, -12.7) * mm});
            skArc(sketch, "E60.5.34", {"start": v(-34.53, -23.21) * mm, "mid": v(-33.78, -23.19) * mm, "end": v(-33.35, -23.8) * mm});
            skLineSegment(sketch, "E60.5.35", {"start": v(-43.9, -24.95) * mm, "end": v(-45.08, -22.89) * mm});
            skArc(sketch, "E60.5.36", {"start": v(-43.33, -10.43) * mm, "mid": v(-43.85, -11.05) * mm, "end": v(-43.55, -11.8) * mm});
            skArc(sketch, "E60.5.37", {"start": v(-37.7, -17.71) * mm, "mid": v(-37.31, -17.08) * mm, "end": v(-37.62, -16.4) * mm});
            skArc(sketch, "E60.5.38", {"start": v(-37.19, -8.7) * mm, "mid": v(-37.54, -8.55) * mm, "end": v(-37.93, -8.58) * mm});
            skArc(sketch, "E60.5.39", {"start": v(-26.43, -11.2) * mm, "mid": v(-26.03, -10.57) * mm, "end": v(-26.34, -9.88) * mm});
            skArc(sketch, "E60.5.40", {"start": v(-42.7, -27.01) * mm, "mid": v(-42.22, -27.38) * mm, "end": v(-41.62, -27.3) * mm});
            skArc(sketch, "E60.5.41", {"start": v(-23.25, -16.7) * mm, "mid": v(-22.5, -16.67) * mm, "end": v(-22.07, -17.28) * mm});
            skArc(sketch, "E60.5.42", {"start": v(-27.12, -1.25) * mm, "mid": v(-27.42, -1.1) * mm, "end": v(-27.75, -1.1) * mm});
            skArc(sketch, "E60.5.43", {"start": v(-20.09, -6.69) * mm, "mid": v(-19.68, -6.85) * mm, "end": v(-19.25, -6.77) * mm});
            skLineSegment(sketch, "E60.5.44", {"start": v(-43.9, -24.95) * mm, "end": v(-42.7, -27.01) * mm});
            skArc(sketch, "E60.5.45", {"start": v(-31.16, -13.36) * mm, "mid": v(-30.73, -13.53) * mm, "end": v(-30.28, -13.42) * mm});
            skArc(sketch, "E60.5.46", {"start": v(-44.8, -21.8) * mm, "mid": v(-45.16, -22.29) * mm, "end": v(-45.08, -22.89) * mm});
            skPoint(sketch, "E60.center", {"position": v(0, 0.4) * mm});
            skArc(sketch, "E61", {"start": v(-3.42, -19.86) * mm, "mid": v(-7.11, -11.93) * mm, "end": v(-15.83, -12.7) * mm});
            skArc(sketch, "E62", {"start": v(-19.25, -6.77) * mm, "mid": v(-14.23, 0.4) * mm, "end": v(-19.25, 7.55) * mm});
            skArc(sketch, "E63", {"start": v(15.83, -12.7) * mm, "mid": v(7.11, -11.93) * mm, "end": v(3.42, -19.86) * mm});
            skArc(sketch, "E64", {"start": v(19.25, 7.55) * mm, "mid": v(14.23, 0.4) * mm, "end": v(19.25, -6.77) * mm});
            skArc(sketch, "E65", {"start": v(-15.83, 13.48) * mm, "mid": v(-7.11, 12.71) * mm, "end": v(-3.42, 20.64) * mm});
            skArc(sketch, "E66", {"start": v(3.42, 20.64) * mm, "mid": v(7.11, 12.71) * mm, "end": v(15.83, 13.48) * mm});
            skSolve(sketch);
        }
        {
            var Q0;
            Q0=makeQuery(id+"F4.imprint","IMPRINT",FACE,{"disambiguationData":[TD([[makeQuery(id+"F4.imprint","IMPRINT",EDGE,{"derivedFrom":sQuery(id+"F4.wireOp",EDGE,"E20")}),-1.0]])]});
            var Q1;
            Q1=qConstructionFilter(qBodyType(qCreatedBy(id+"F4",EDGE),BodyType.WIRE),ConstructionObject.NO);
            extrude(context, id + "F5", {"entities" : qUnion([Q0]), "surfaceEntities" : qUnion([Q1]), "oppositeDirection" : true, "depth" : 25.4 * mm});
        }
        {
            var Q0;
            Q0=qSketchRegion(id+"F0",true);
            extrude(context, id + "F6", {"entities" : qUnion([Q0]), "operationType" : NewBodyOperationType.REMOVE, "depth" : 22.22 * mm});
        }
        {
            var Q0;
            Q0=makeQuery(id+"F5.opExtrude","CAP_FACE",FACE,{"disambiguationData":[OSD([sQuery(id+"F0.wireOp",EDGE,"E0"),sQuery(id+"F2.wireOp",EDGE,"E4"),sQuery(id+"F2.wireOp",EDGE,"E5"),sQuery(id+"F2.wireOp",EDGE,"E6"),sQuery(id+"F2.wireOp",EDGE,"E7"),sQuery(id+"F2.wireOp",EDGE,"E11.filletArc"),sQuery(id+"F2.wireOp",EDGE,"E12.filletArc"),sQuery(id+"F2.wireOp",EDGE,"E13.filletArc"),sQuery(id+"F2.wireOp",EDGE,"E14.filletArc"),sQuery(id+"F2.wireOp",EDGE,"E15.1.0"),sQuery(id+"F2.wireOp",EDGE,"E15.1.1"),sQuery(id+"F2.wireOp",EDGE,"E15.1.2"),sQuery(id+"F2.wireOp",EDGE,"E15.1.3"),sQuery(id+"F2.wireOp",EDGE,"E15.1.4"),sQuery(id+"F2.wireOp",EDGE,"E15.1.5"),sQuery(id+"F2.wireOp",EDGE,"E15.1.6"),sQuery(id+"F2.wireOp",EDGE,"E15.1.7"),sQuery(id+"F2.wireOp",EDGE,"E15.2.0"),sQuery(id+"F2.wireOp",EDGE,"E15.2.1"),sQuery(id+"F2.wireOp",EDGE,"E15.2.2"),sQuery(id+"F2.wireOp",EDGE,"E15.2.3"),sQuery(id+"F2.wireOp",EDGE,"E15.2.4"),sQuery(id+"F2.wireOp",EDGE,"E15.2.5"),sQuery(id+"F2.wireOp",EDGE,"E15.2.6"),sQuery(id+"F2.wireOp",EDGE,"E15.2.7"),sQuery(id+"F2.wireOp",EDGE,"E15.3.0"),sQuery(id+"F2.wireOp",EDGE,"E15.3.1"),sQuery(id+"F2.wireOp",EDGE,"E15.3.2"),sQuery(id+"F2.wireOp",EDGE,"E15.3.3"),sQuery(id+"F2.wireOp",EDGE,"E15.3.4"),sQuery(id+"F2.wireOp",EDGE,"E15.3.5"),sQuery(id+"F2.wireOp",EDGE,"E15.3.6"),sQuery(id+"F2.wireOp",EDGE,"E15.3.7"),sQuery(id+"F2.wireOp",EDGE,"E15.4.0"),sQuery(id+"F2.wireOp",EDGE,"E15.4.1"),sQuery(id+"F2.wireOp",EDGE,"E15.4.2"),sQuery(id+"F2.wireOp",EDGE,"E15.4.3"),sQuery(id+"F2.wireOp",EDGE,"E15.4.4"),sQuery(id+"F2.wireOp",EDGE,"E15.4.5"),sQuery(id+"F2.wireOp",EDGE,"E15.4.6"),sQuery(id+"F2.wireOp",EDGE,"E15.4.7"),sQuery(id+"F2.wireOp",EDGE,"E15.5.0"),sQuery(id+"F2.wireOp",EDGE,"E15.5.1"),sQuery(id+"F2.wireOp",EDGE,"E15.5.2"),sQuery(id+"F2.wireOp",EDGE,"E15.5.3"),sQuery(id+"F2.wireOp",EDGE,"E15.5.4"),sQuery(id+"F2.wireOp",EDGE,"E15.5.5"),sQuery(id+"F2.wireOp",EDGE,"E15.5.6"),sQuery(id+"F2.wireOp",EDGE,"E15.5.7"),sQuery(id+"F4.wireOp",EDGE,"E20"),sQuery(id+"F4.wireOp",EDGE,"E21"),sQuery(id+"F4.wireOp",EDGE,"E22"),sQuery(id+"F4.wireOp",EDGE,"E23"),sQuery(id+"F4.wireOp",EDGE,"E24"),sQuery(id+"F4.wireOp",EDGE,"E25"),sQuery(id+"F4.wireOp",EDGE,"E26"),sQuery(id+"F4.wireOp",EDGE,"E27"),sQuery(id+"F4.wireOp",EDGE,"E28"),sQuery(id+"F4.wireOp",EDGE,"E31.filletArc"),sQuery(id+"F4.wireOp",EDGE,"E32.filletArc"),sQuery(id+"F4.wireOp",EDGE,"E33.filletArc"),sQuery(id+"F4.wireOp",EDGE,"E34.filletArc"),sQuery(id+"F4.wireOp",EDGE,"E35.filletArc"),sQuery(id+"F4.wireOp",EDGE,"E36.filletArc"),sQuery(id+"F4.wireOp",EDGE,"E37.filletArc"),sQuery(id+"F4.wireOp",EDGE,"E38.filletArc"),sQuery(id+"F4.wireOp",EDGE,"E41.MirrorCS"),sQuery(id+"F4.wireOp",EDGE,"E42.MirrorCS"),sQuery(id+"F4.wireOp",EDGE,"E43.MirrorCS"),sQuery(id+"F4.wireOp",EDGE,"E44.MirrorCS"),sQuery(id+"F4.wireOp",EDGE,"E45.MirrorCS"),sQuery(id+"F4.wireOp",EDGE,"E46.MirrorCS"),sQuery(id+"F4.wireOp",EDGE,"E47.MirrorCS"),sQuery(id+"F4.wireOp",EDGE,"E48.MirrorCS"),sQuery(id+"F4.wireOp",EDGE,"E49.MirrorCS"),sQuery(id+"F4.wireOp",EDGE,"E50.MirrorCS"),sQuery(id+"F4.wireOp",EDGE,"E51.MirrorCS"),sQuery(id+"F4.wireOp",EDGE,"E52.MirrorCS"),sQuery(id+"F4.wireOp",EDGE,"E53.MirrorCS"),sQuery(id+"F4.wireOp",EDGE,"E54.MirrorCS"),sQuery(id+"F4.wireOp",EDGE,"E55.MirrorCS"),sQuery(id+"F4.wireOp",EDGE,"E56.MirrorCS"),sQuery(id+"F4.wireOp",EDGE,"E57.MirrorCS"),sQuery(id+"F4.wireOp",EDGE,"E58.filletArc"),sQuery(id+"F4.wireOp",EDGE,"E59.filletArc"),sQuery(id+"F4.wireOp",EDGE,"E60.1.0"),sQuery(id+"F4.wireOp",EDGE,"E60.1.1"),sQuery(id+"F4.wireOp",EDGE,"E60.1.2"),sQuery(id+"F4.wireOp",EDGE,"E60.1.4"),sQuery(id+"F4.wireOp",EDGE,"E60.1.5"),sQuery(id+"F4.wireOp",EDGE,"E60.1.6"),sQuery(id+"F4.wireOp",EDGE,"E60.1.7"),sQuery(id+"F4.wireOp",EDGE,"E60.1.11"),sQuery(id+"F4.wireOp",EDGE,"E60.1.13"),sQuery(id+"F4.wireOp",EDGE,"E60.1.15"),sQuery(id+"F4.wireOp",EDGE,"E60.1.16"),sQuery(id+"F4.wireOp",EDGE,"E60.1.18"),sQuery(id+"F4.wireOp",EDGE,"E60.1.21"),sQuery(id+"F4.wireOp",EDGE,"E60.1.22"),sQuery(id+"F4.wireOp",EDGE,"E60.1.23"),sQuery(id+"F4.wireOp",EDGE,"E60.1.25"),sQuery(id+"F4.wireOp",EDGE,"E60.1.27"),sQuery(id+"F4.wireOp",EDGE,"E60.1.28"),sQuery(id+"F4.wireOp",EDGE,"E60.1.29"),sQuery(id+"F4.wireOp",EDGE,"E60.1.30"),sQuery(id+"F4.wireOp",EDGE,"E60.1.31"),sQuery(id+"F4.wireOp",EDGE,"E60.1.32"),sQuery(id+"F4.wireOp",EDGE,"E60.1.33"),sQuery(id+"F4.wireOp",EDGE,"E60.1.34"),sQuery(id+"F4.wireOp",EDGE,"E60.1.35"),sQuery(id+"F4.wireOp",EDGE,"E60.1.36"),sQuery(id+"F4.wireOp",EDGE,"E60.1.37"),sQuery(id+"F4.wireOp",EDGE,"E60.1.38"),sQuery(id+"F4.wireOp",EDGE,"E60.1.39"),sQuery(id+"F4.wireOp",EDGE,"E60.1.40"),sQuery(id+"F4.wireOp",EDGE,"E60.1.41"),sQuery(id+"F4.wireOp",EDGE,"E60.1.42"),sQuery(id+"F4.wireOp",EDGE,"E60.1.43"),sQuery(id+"F4.wireOp",EDGE,"E60.1.44"),sQuery(id+"F4.wireOp",EDGE,"E60.1.45"),sQuery(id+"F4.wireOp",EDGE,"E60.1.46"),sQuery(id+"F4.wireOp",EDGE,"E60.2.0"),sQuery(id+"F4.wireOp",EDGE,"E60.2.1"),sQuery(id+"F4.wireOp",EDGE,"E60.2.2"),sQuery(id+"F4.wireOp",EDGE,"E60.2.4"),sQuery(id+"F4.wireOp",EDGE,"E60.2.5"),sQuery(id+"F4.wireOp",EDGE,"E60.2.6"),sQuery(id+"F4.wireOp",EDGE,"E60.2.7"),sQuery(id+"F4.wireOp",EDGE,"E60.2.11"),sQuery(id+"F4.wireOp",EDGE,"E60.2.13"),sQuery(id+"F4.wireOp",EDGE,"E60.2.15"),sQuery(id+"F4.wireOp",EDGE,"E60.2.16"),sQuery(id+"F4.wireOp",EDGE,"E60.2.18"),sQuery(id+"F4.wireOp",EDGE,"E60.2.21"),sQuery(id+"F4.wireOp",EDGE,"E60.2.22"),sQuery(id+"F4.wireOp",EDGE,"E60.2.23"),sQuery(id+"F4.wireOp",EDGE,"E60.2.25"),sQuery(id+"F4.wireOp",EDGE,"E60.2.27"),sQuery(id+"F4.wireOp",EDGE,"E60.2.28"),sQuery(id+"F4.wireOp",EDGE,"E60.2.29"),sQuery(id+"F4.wireOp",EDGE,"E60.2.30"),sQuery(id+"F4.wireOp",EDGE,"E60.2.31"),sQuery(id+"F4.wireOp",EDGE,"E60.2.32"),sQuery(id+"F4.wireOp",EDGE,"E60.2.33"),sQuery(id+"F4.wireOp",EDGE,"E60.2.34"),sQuery(id+"F4.wireOp",EDGE,"E60.2.35"),sQuery(id+"F4.wireOp",EDGE,"E60.2.36"),sQuery(id+"F4.wireOp",EDGE,"E60.2.37"),sQuery(id+"F4.wireOp",EDGE,"E60.2.38"),sQuery(id+"F4.wireOp",EDGE,"E60.2.39"),sQuery(id+"F4.wireOp",EDGE,"E60.2.40"),sQuery(id+"F4.wireOp",EDGE,"E60.2.41"),sQuery(id+"F4.wireOp",EDGE,"E60.2.42"),sQuery(id+"F4.wireOp",EDGE,"E60.2.43"),sQuery(id+"F4.wireOp",EDGE,"E60.2.44"),sQuery(id+"F4.wireOp",EDGE,"E60.2.45"),sQuery(id+"F4.wireOp",EDGE,"E60.2.46"),sQuery(id+"F4.wireOp",EDGE,"E60.3.0"),sQuery(id+"F4.wireOp",EDGE,"E60.3.1"),sQuery(id+"F4.wireOp",EDGE,"E60.3.2"),sQuery(id+"F4.wireOp",EDGE,"E60.3.4"),sQuery(id+"F4.wireOp",EDGE,"E60.3.5"),sQuery(id+"F4.wireOp",EDGE,"E60.3.6"),sQuery(id+"F4.wireOp",EDGE,"E60.3.7"),sQuery(id+"F4.wireOp",EDGE,"E60.3.11"),sQuery(id+"F4.wireOp",EDGE,"E60.3.13"),sQuery(id+"F4.wireOp",EDGE,"E60.3.15"),sQuery(id+"F4.wireOp",EDGE,"E60.3.16"),sQuery(id+"F4.wireOp",EDGE,"E60.3.18"),sQuery(id+"F4.wireOp",EDGE,"E60.3.21"),sQuery(id+"F4.wireOp",EDGE,"E60.3.22"),sQuery(id+"F4.wireOp",EDGE,"E60.3.23"),sQuery(id+"F4.wireOp",EDGE,"E60.3.25"),sQuery(id+"F4.wireOp",EDGE,"E60.3.27"),sQuery(id+"F4.wireOp",EDGE,"E60.3.28"),sQuery(id+"F4.wireOp",EDGE,"E60.3.29"),sQuery(id+"F4.wireOp",EDGE,"E60.3.30"),sQuery(id+"F4.wireOp",EDGE,"E60.3.31"),sQuery(id+"F4.wireOp",EDGE,"E60.3.32"),sQuery(id+"F4.wireOp",EDGE,"E60.3.33"),sQuery(id+"F4.wireOp",EDGE,"E60.3.34"),sQuery(id+"F4.wireOp",EDGE,"E60.3.35"),sQuery(id+"F4.wireOp",EDGE,"E60.3.36"),sQuery(id+"F4.wireOp",EDGE,"E60.3.37"),sQuery(id+"F4.wireOp",EDGE,"E60.3.38"),sQuery(id+"F4.wireOp",EDGE,"E60.3.39"),sQuery(id+"F4.wireOp",EDGE,"E60.3.40"),sQuery(id+"F4.wireOp",EDGE,"E60.3.41"),sQuery(id+"F4.wireOp",EDGE,"E60.3.42"),sQuery(id+"F4.wireOp",EDGE,"E60.3.43"),sQuery(id+"F4.wireOp",EDGE,"E60.3.44"),sQuery(id+"F4.wireOp",EDGE,"E60.3.45"),sQuery(id+"F4.wireOp",EDGE,"E60.3.46"),sQuery(id+"F4.wireOp",EDGE,"E60.4.0"),sQuery(id+"F4.wireOp",EDGE,"E60.4.1"),sQuery(id+"F4.wireOp",EDGE,"E60.4.2"),sQuery(id+"F4.wireOp",EDGE,"E60.4.4"),sQuery(id+"F4.wireOp",EDGE,"E60.4.5"),sQuery(id+"F4.wireOp",EDGE,"E60.4.6"),sQuery(id+"F4.wireOp",EDGE,"E60.4.7"),sQuery(id+"F4.wireOp",EDGE,"E60.4.11"),sQuery(id+"F4.wireOp",EDGE,"E60.4.13"),sQuery(id+"F4.wireOp",EDGE,"E60.4.15"),sQuery(id+"F4.wireOp",EDGE,"E60.4.16"),sQuery(id+"F4.wireOp",EDGE,"E60.4.18"),sQuery(id+"F4.wireOp",EDGE,"E60.4.21"),sQuery(id+"F4.wireOp",EDGE,"E60.4.22"),sQuery(id+"F4.wireOp",EDGE,"E60.4.23"),sQuery(id+"F4.wireOp",EDGE,"E60.4.25"),sQuery(id+"F4.wireOp",EDGE,"E60.4.27"),sQuery(id+"F4.wireOp",EDGE,"E60.4.28"),sQuery(id+"F4.wireOp",EDGE,"E60.4.29"),sQuery(id+"F4.wireOp",EDGE,"E60.4.30"),sQuery(id+"F4.wireOp",EDGE,"E60.4.31"),sQuery(id+"F4.wireOp",EDGE,"E60.4.32"),sQuery(id+"F4.wireOp",EDGE,"E60.4.33"),sQuery(id+"F4.wireOp",EDGE,"E60.4.34"),sQuery(id+"F4.wireOp",EDGE,"E60.4.35"),sQuery(id+"F4.wireOp",EDGE,"E60.4.36"),sQuery(id+"F4.wireOp",EDGE,"E60.4.37"),sQuery(id+"F4.wireOp",EDGE,"E60.4.38"),sQuery(id+"F4.wireOp",EDGE,"E60.4.39"),sQuery(id+"F4.wireOp",EDGE,"E60.4.40"),sQuery(id+"F4.wireOp",EDGE,"E60.4.41"),sQuery(id+"F4.wireOp",EDGE,"E60.4.42"),sQuery(id+"F4.wireOp",EDGE,"E60.4.43"),sQuery(id+"F4.wireOp",EDGE,"E60.4.44"),sQuery(id+"F4.wireOp",EDGE,"E60.4.45"),sQuery(id+"F4.wireOp",EDGE,"E60.4.46"),sQuery(id+"F4.wireOp",EDGE,"E60.5.0"),sQuery(id+"F4.wireOp",EDGE,"E60.5.1"),sQuery(id+"F4.wireOp",EDGE,"E60.5.2"),sQuery(id+"F4.wireOp",EDGE,"E60.5.4"),sQuery(id+"F4.wireOp",EDGE,"E60.5.5"),sQuery(id+"F4.wireOp",EDGE,"E60.5.6"),sQuery(id+"F4.wireOp",EDGE,"E60.5.7"),sQuery(id+"F4.wireOp",EDGE,"E60.5.11"),sQuery(id+"F4.wireOp",EDGE,"E60.5.13"),sQuery(id+"F4.wireOp",EDGE,"E60.5.15"),sQuery(id+"F4.wireOp",EDGE,"E60.5.16"),sQuery(id+"F4.wireOp",EDGE,"E60.5.18"),sQuery(id+"F4.wireOp",EDGE,"E60.5.21"),sQuery(id+"F4.wireOp",EDGE,"E60.5.22"),sQuery(id+"F4.wireOp",EDGE,"E60.5.23"),sQuery(id+"F4.wireOp",EDGE,"E60.5.25"),sQuery(id+"F4.wireOp",EDGE,"E60.5.27"),sQuery(id+"F4.wireOp",EDGE,"E60.5.28"),sQuery(id+"F4.wireOp",EDGE,"E60.5.29"),sQuery(id+"F4.wireOp",EDGE,"E60.5.30"),sQuery(id+"F4.wireOp",EDGE,"E60.5.31"),sQuery(id+"F4.wireOp",EDGE,"E60.5.32"),sQuery(id+"F4.wireOp",EDGE,"E60.5.33"),sQuery(id+"F4.wireOp",EDGE,"E60.5.34"),sQuery(id+"F4.wireOp",EDGE,"E60.5.35"),sQuery(id+"F4.wireOp",EDGE,"E60.5.36"),sQuery(id+"F4.wireOp",EDGE,"E60.5.37"),sQuery(id+"F4.wireOp",EDGE,"E60.5.38"),sQuery(id+"F4.wireOp",EDGE,"E60.5.39"),sQuery(id+"F4.wireOp",EDGE,"E60.5.40"),sQuery(id+"F4.wireOp",EDGE,"E60.5.41"),sQuery(id+"F4.wireOp",EDGE,"E60.5.42"),sQuery(id+"F4.wireOp",EDGE,"E60.5.43"),sQuery(id+"F4.wireOp",EDGE,"E60.5.44"),sQuery(id+"F4.wireOp",EDGE,"E60.5.45"),sQuery(id+"F4.wireOp",EDGE,"E60.5.46"),sQuery(id+"F4.wireOp",EDGE,"E61"),sQuery(id+"F4.wireOp",EDGE,"E62"),sQuery(id+"F4.wireOp",EDGE,"E63"),sQuery(id+"F4.wireOp",EDGE,"E64"),sQuery(id+"F4.wireOp",EDGE,"E65"),sQuery(id+"F4.wireOp",EDGE,"E66")])],"isStart":false});
            var sketch = newSketch(context, id + "F7", { "sketchPlane" : qUnion([Q0])});
            skArc(sketch, "E67", {"start": v(3.18, 46.92) * mm, "mid": v(-0.15, 59.12) * mm, "end": v(-3.17, 46.84) * mm});
            skCircle(sketch, "E68", {"center": v(0, 0) * mm, "radius": 10.24 * mm, "construction": true});
            skCircle(sketch, "E69", {"center": v(-0.07, 52.59) * mm, "radius": 6.53 * mm});
            skCircle(sketch, "E70.1.0", {"center": v(-45.58, 26.23) * mm, "radius": 6.53 * mm});
            skCircle(sketch, "E70.2.0", {"center": v(-45.5, -26.36) * mm, "radius": 6.53 * mm});
            skCircle(sketch, "E70.3.0", {"center": v(0.07, -52.59) * mm, "radius": 6.53 * mm});
            skCircle(sketch, "E70.4.0", {"center": v(45.58, -26.23) * mm, "radius": 6.53 * mm});
            skCircle(sketch, "E70.5.0", {"center": v(45.5, 26.36) * mm, "radius": 6.53 * mm});
            skCircle(sketch, "E71", {"center": v(-0.07, 52.59) * mm, "radius": 3.36 * mm});
            skCircle(sketch, "E72.1.0", {"center": v(-45.58, 26.23) * mm, "radius": 3.36 * mm});
            skCircle(sketch, "E72.2.0", {"center": v(-45.5, -26.36) * mm, "radius": 3.36 * mm});
            skCircle(sketch, "E73.1.3.0", {"center": v(0.07, -52.59) * mm, "radius": 3.36 * mm});
            skCircle(sketch, "E73.1.4.0", {"center": v(45.58, -26.23) * mm, "radius": 3.36 * mm});
            skCircle(sketch, "E73.1.5.0", {"center": v(45.5, 26.36) * mm, "radius": 3.36 * mm});
            skSolve(sketch);
        }
        {
            var Q0;
            {var subQ6=makeQuery(id+"F5.opExtrude","CAP_EDGE",EDGE,{"disambiguationData":[OSD([sQuery(id+"F4.wireOp",EDGE,"E58.filletArc")])],"isStart":false});Q0=makeQuery(id+"F7.imprint","IMPRINT",FACE,{"disambiguationData":[TD([[makeQuery(id+"F7.imprint","IMPRINT",EDGE,{"derivedFrom":subQ6}),1.0]])]});}
            extrude(context, id + "F8", {"entities" : qUnion([Q0]), "operationType" : NewBodyOperationType.ADD, "oppositeDirection" : true, "depth" : 3.17 * mm});
        }
        {
            var Q0;
            {var subQ0=makeQuery(id+"F5.opExtrude","CAP_EDGE",EDGE,{"disambiguationData":[OSD([sQuery(id+"F4.wireOp",EDGE,"E60.1.40")])],"isStart":false});Q0=makeQuery(id+"F7.imprint","IMPRINT",FACE,{"disambiguationData":[TD([[makeQuery(id+"F7.imprint","IMPRINT",EDGE,{"derivedFrom":subQ0}),1.0]])]});}
            var Q1;
            {var subQ3=sQuery(id+"F7.wireOp",EDGE,"E70.4.0");var subQ6=makeQuery(id+"F5.opExtrude","CAP_EDGE",EDGE,{"disambiguationData":[OSD([sQuery(id+"F4.wireOp",EDGE,"E60.2.2")])],"isStart":false});var subQ8=makeQuery(id+"F7.imprint","INTERSECT",VERTEX,{"derivedFrom":[subQ6,subQ3]});Q1=makeQuery(id+"F7.imprint","IMPRINT",FACE,{"disambiguationData":[TD([[makeQuery(id+"F7.imprint","IMPRINT",EDGE,{"disambiguationData":[TD([[subQ8,-1.0]])],"derivedFrom":subQ3}),1.0]])]});}
            var Q2;
            {var subQ0=makeQuery(id+"F5.opExtrude","CAP_EDGE",EDGE,{"disambiguationData":[OSD([sQuery(id+"F4.wireOp",EDGE,"E59.filletArc")])],"isStart":false});Q2=makeQuery(id+"F7.imprint","IMPRINT",FACE,{"disambiguationData":[TD([[makeQuery(id+"F7.imprint","IMPRINT",EDGE,{"derivedFrom":subQ0}),1.0]])]});}
            var Q3;
            {var subQ5=makeQuery(id+"F5.opExtrude","CAP_EDGE",EDGE,{"disambiguationData":[OSD([sQuery(id+"F4.wireOp",EDGE,"E60.5.46")])],"isStart":false});Q3=makeQuery(id+"F7.imprint","IMPRINT",FACE,{"disambiguationData":[TD([[makeQuery(id+"F7.imprint","IMPRINT",EDGE,{"derivedFrom":subQ5}),1.0]])]});}
            var Q4;
            {var subQ3=sQuery(id+"F7.wireOp",EDGE,"E70.2.0");var subQ6=makeQuery(id+"F5.opExtrude","CAP_EDGE",EDGE,{"disambiguationData":[OSD([sQuery(id+"F4.wireOp",EDGE,"E60.4.2")])],"isStart":false});var subQ8=makeQuery(id+"F7.imprint","INTERSECT",VERTEX,{"derivedFrom":[subQ6,subQ3]});Q4=makeQuery(id+"F7.imprint","IMPRINT",FACE,{"disambiguationData":[TD([[makeQuery(id+"F7.imprint","IMPRINT",EDGE,{"disambiguationData":[TD([[subQ8,-1.0]])],"derivedFrom":subQ3}),1.0]])]});}
            var Q5;
            Q5=sQuery(id+"F7.wireOp",EDGE,"E70.5.0");
            extrude(context, id + "F9", {"entities" : qUnion([Q0, Q1, Q2, Q3, Q4]), "operationType" : NewBodyOperationType.ADD, "surfaceEntities" : qUnion([Q5]), "oppositeDirection" : true, "depth" : 3.17 * mm});
        }
        {
            var Q0;
            {var subQ5=makeQuery(id+"F5.opExtrude","CAP_EDGE",EDGE,{"disambiguationData":[OSD([sQuery(id+"F4.wireOp",EDGE,"E60.2.35"),sQuery(id+"F4.wireOp",EDGE,"E60.2.44")])],"isStart":false});Q0=makeQuery(id+"F7.imprint","IMPRINT",FACE,{"disambiguationData":[TD([[makeQuery(id+"F7.imprint","IMPRINT",EDGE,{"derivedFrom":subQ5}),1.0]])]});}
            var Q1;
            {var subQ0=sQuery(id+"F7.wireOp",EDGE,"E73.1.5.0");var subQ3=makeQuery(id+"F5.opExtrude","CAP_EDGE",EDGE,{"disambiguationData":[OSD([sQuery(id+"F4.wireOp",EDGE,"E60.1.46")])],"isStart":false});var subQ4=makeQuery(id+"F7.imprint","INTERSECT",VERTEX,{"derivedFrom":[subQ3,subQ0]});Q1=makeQuery(id+"F7.imprint","IMPRINT",FACE,{"disambiguationData":[TD([[makeQuery(id+"F7.imprint","IMPRINT",EDGE,{"disambiguationData":[TD([[subQ4,-1.0]])],"derivedFrom":subQ0}),1.0]])]});}
            var Q2;
            {var subQ1=makeQuery(id+"F5.opExtrude","CAP_EDGE",EDGE,{"disambiguationData":[OSD([sQuery(id+"F4.wireOp",EDGE,"E20"),sQuery(id+"F4.wireOp",EDGE,"E41.MirrorCS")])],"isStart":false});Q2=makeQuery(id+"F7.imprint","IMPRINT",FACE,{"disambiguationData":[TD([[makeQuery(id+"F7.imprint","IMPRINT",EDGE,{"derivedFrom":subQ1}),-1.0]])]});}
            var Q3;
            {var subQ1=makeQuery(id+"F5.opExtrude","CAP_EDGE",EDGE,{"disambiguationData":[OSD([sQuery(id+"F4.wireOp",EDGE,"E20"),sQuery(id+"F4.wireOp",EDGE,"E41.MirrorCS")])],"isStart":false});Q3=makeQuery(id+"F7.imprint","IMPRINT",FACE,{"disambiguationData":[TD([[makeQuery(id+"F7.imprint","IMPRINT",EDGE,{"derivedFrom":subQ1}),1.0]])]});}
            var Q4;
            {var subQ0=sQuery(id+"F7.wireOp",EDGE,"E72.1.0");var subQ3=makeQuery(id+"F5.opExtrude","CAP_EDGE",EDGE,{"disambiguationData":[OSD([sQuery(id+"F4.wireOp",EDGE,"E60.5.40")])],"isStart":false});var subQ4=makeQuery(id+"F7.imprint","INTERSECT",VERTEX,{"derivedFrom":[subQ3,subQ0]});Q4=makeQuery(id+"F7.imprint","IMPRINT",FACE,{"disambiguationData":[TD([[makeQuery(id+"F7.imprint","IMPRINT",EDGE,{"disambiguationData":[TD([[subQ4,1.0]])],"derivedFrom":subQ0}),1.0]])]});}
            var Q5;
            {var subQ5=makeQuery(id+"F5.opExtrude","CAP_EDGE",EDGE,{"disambiguationData":[OSD([sQuery(id+"F4.wireOp",EDGE,"E60.4.35"),sQuery(id+"F4.wireOp",EDGE,"E60.4.44")])],"isStart":false});Q5=makeQuery(id+"F7.imprint","IMPRINT",FACE,{"disambiguationData":[TD([[makeQuery(id+"F7.imprint","IMPRINT",EDGE,{"derivedFrom":subQ5}),1.0]])]});}
            extrude(context, id + "F10", {"entities" : qUnion([Q0, Q1, Q2, Q3, Q4, Q5]), "operationType" : NewBodyOperationType.REMOVE, "oppositeDirection" : true, "depth" : 25.4 * mm});
        }
        {
            var Q0;
            Q0=makeQuery(id+"F5.opExtrude","SWEPT_BODY",BODY,{"disambiguationData":[OSD([sQuery(id+"F2.wireOp",EDGE,"E4"),sQuery(id+"F2.wireOp",EDGE,"E5"),sQuery(id+"F2.wireOp",EDGE,"E6"),sQuery(id+"F2.wireOp",EDGE,"E7"),sQuery(id+"F2.wireOp",EDGE,"E11.filletArc"),sQuery(id+"F2.wireOp",EDGE,"E12.filletArc"),sQuery(id+"F2.wireOp",EDGE,"E13.filletArc"),sQuery(id+"F2.wireOp",EDGE,"E14.filletArc"),sQuery(id+"F2.wireOp",EDGE,"E15.1.0"),sQuery(id+"F2.wireOp",EDGE,"E15.1.1"),sQuery(id+"F2.wireOp",EDGE,"E15.1.2"),sQuery(id+"F2.wireOp",EDGE,"E15.1.3"),sQuery(id+"F2.wireOp",EDGE,"E15.1.4"),sQuery(id+"F2.wireOp",EDGE,"E15.1.5"),sQuery(id+"F2.wireOp",EDGE,"E15.1.6"),sQuery(id+"F2.wireOp",EDGE,"E15.1.7"),sQuery(id+"F2.wireOp",EDGE,"E15.2.0"),sQuery(id+"F2.wireOp",EDGE,"E15.2.1"),sQuery(id+"F2.wireOp",EDGE,"E15.2.2"),sQuery(id+"F2.wireOp",EDGE,"E15.2.3"),sQuery(id+"F2.wireOp",EDGE,"E15.2.4"),sQuery(id+"F2.wireOp",EDGE,"E15.2.5"),sQuery(id+"F2.wireOp",EDGE,"E15.2.6"),sQuery(id+"F2.wireOp",EDGE,"E15.2.7"),sQuery(id+"F2.wireOp",EDGE,"E15.3.0"),sQuery(id+"F2.wireOp",EDGE,"E15.3.1"),sQuery(id+"F2.wireOp",EDGE,"E15.3.2"),sQuery(id+"F2.wireOp",EDGE,"E15.3.3"),sQuery(id+"F2.wireOp",EDGE,"E15.3.4"),sQuery(id+"F2.wireOp",EDGE,"E15.3.5"),sQuery(id+"F2.wireOp",EDGE,"E15.3.6"),sQuery(id+"F2.wireOp",EDGE,"E15.3.7"),sQuery(id+"F2.wireOp",EDGE,"E15.4.0"),sQuery(id+"F2.wireOp",EDGE,"E15.4.1"),sQuery(id+"F2.wireOp",EDGE,"E15.4.2"),sQuery(id+"F2.wireOp",EDGE,"E15.4.3"),sQuery(id+"F2.wireOp",EDGE,"E15.4.4"),sQuery(id+"F2.wireOp",EDGE,"E15.4.5"),sQuery(id+"F2.wireOp",EDGE,"E15.4.6"),sQuery(id+"F2.wireOp",EDGE,"E15.4.7"),sQuery(id+"F2.wireOp",EDGE,"E15.5.0"),sQuery(id+"F2.wireOp",EDGE,"E15.5.1"),sQuery(id+"F2.wireOp",EDGE,"E15.5.2"),sQuery(id+"F2.wireOp",EDGE,"E15.5.3"),sQuery(id+"F2.wireOp",EDGE,"E15.5.4"),sQuery(id+"F2.wireOp",EDGE,"E15.5.5"),sQuery(id+"F2.wireOp",EDGE,"E15.5.6"),sQuery(id+"F2.wireOp",EDGE,"E15.5.7"),sQuery(id+"F4.wireOp",EDGE,"E20"),sQuery(id+"F4.wireOp",EDGE,"E21"),sQuery(id+"F4.wireOp",EDGE,"E22"),sQuery(id+"F4.wireOp",EDGE,"E23"),sQuery(id+"F4.wireOp",EDGE,"E24"),sQuery(id+"F4.wireOp",EDGE,"E25"),sQuery(id+"F4.wireOp",EDGE,"E26"),sQuery(id+"F4.wireOp",EDGE,"E27"),sQuery(id+"F4.wireOp",EDGE,"E28"),sQuery(id+"F4.wireOp",EDGE,"E31.filletArc"),sQuery(id+"F4.wireOp",EDGE,"E32.filletArc"),sQuery(id+"F4.wireOp",EDGE,"E33.filletArc"),sQuery(id+"F4.wireOp",EDGE,"E34.filletArc"),sQuery(id+"F4.wireOp",EDGE,"E35.filletArc"),sQuery(id+"F4.wireOp",EDGE,"E36.filletArc"),sQuery(id+"F4.wireOp",EDGE,"E37.filletArc"),sQuery(id+"F4.wireOp",EDGE,"E38.filletArc"),sQuery(id+"F4.wireOp",EDGE,"E41.MirrorCS"),sQuery(id+"F4.wireOp",EDGE,"E42.MirrorCS"),sQuery(id+"F4.wireOp",EDGE,"E43.MirrorCS"),sQuery(id+"F4.wireOp",EDGE,"E44.MirrorCS"),sQuery(id+"F4.wireOp",EDGE,"E45.MirrorCS"),sQuery(id+"F4.wireOp",EDGE,"E46.MirrorCS"),sQuery(id+"F4.wireOp",EDGE,"E47.MirrorCS"),sQuery(id+"F4.wireOp",EDGE,"E48.MirrorCS"),sQuery(id+"F4.wireOp",EDGE,"E49.MirrorCS"),sQuery(id+"F4.wireOp",EDGE,"E50.MirrorCS"),sQuery(id+"F4.wireOp",EDGE,"E51.MirrorCS"),sQuery(id+"F4.wireOp",EDGE,"E52.MirrorCS"),sQuery(id+"F4.wireOp",EDGE,"E53.MirrorCS"),sQuery(id+"F4.wireOp",EDGE,"E54.MirrorCS"),sQuery(id+"F4.wireOp",EDGE,"E55.MirrorCS"),sQuery(id+"F4.wireOp",EDGE,"E56.MirrorCS"),sQuery(id+"F4.wireOp",EDGE,"E57.MirrorCS"),sQuery(id+"F4.wireOp",EDGE,"E58.filletArc"),sQuery(id+"F4.wireOp",EDGE,"E59.filletArc"),sQuery(id+"F4.wireOp",EDGE,"E60.1.0"),sQuery(id+"F4.wireOp",EDGE,"E60.1.1"),sQuery(id+"F4.wireOp",EDGE,"E60.1.2"),sQuery(id+"F4.wireOp",EDGE,"E60.1.4"),sQuery(id+"F4.wireOp",EDGE,"E60.1.5"),sQuery(id+"F4.wireOp",EDGE,"E60.1.6"),sQuery(id+"F4.wireOp",EDGE,"E60.1.7"),sQuery(id+"F4.wireOp",EDGE,"E60.1.11"),sQuery(id+"F4.wireOp",EDGE,"E60.1.13"),sQuery(id+"F4.wireOp",EDGE,"E60.1.15"),sQuery(id+"F4.wireOp",EDGE,"E60.1.16"),sQuery(id+"F4.wireOp",EDGE,"E60.1.18"),sQuery(id+"F4.wireOp",EDGE,"E60.1.21"),sQuery(id+"F4.wireOp",EDGE,"E60.1.22"),sQuery(id+"F4.wireOp",EDGE,"E60.1.23"),sQuery(id+"F4.wireOp",EDGE,"E60.1.25"),sQuery(id+"F4.wireOp",EDGE,"E60.1.27"),sQuery(id+"F4.wireOp",EDGE,"E60.1.28"),sQuery(id+"F4.wireOp",EDGE,"E60.1.29"),sQuery(id+"F4.wireOp",EDGE,"E60.1.30"),sQuery(id+"F4.wireOp",EDGE,"E60.1.31"),sQuery(id+"F4.wireOp",EDGE,"E60.1.32"),sQuery(id+"F4.wireOp",EDGE,"E60.1.33"),sQuery(id+"F4.wireOp",EDGE,"E60.1.34"),sQuery(id+"F4.wireOp",EDGE,"E60.1.35"),sQuery(id+"F4.wireOp",EDGE,"E60.1.36"),sQuery(id+"F4.wireOp",EDGE,"E60.1.37"),sQuery(id+"F4.wireOp",EDGE,"E60.1.38"),sQuery(id+"F4.wireOp",EDGE,"E60.1.39"),sQuery(id+"F4.wireOp",EDGE,"E60.1.40"),sQuery(id+"F4.wireOp",EDGE,"E60.1.41"),sQuery(id+"F4.wireOp",EDGE,"E60.1.42"),sQuery(id+"F4.wireOp",EDGE,"E60.1.43"),sQuery(id+"F4.wireOp",EDGE,"E60.1.44"),sQuery(id+"F4.wireOp",EDGE,"E60.1.45"),sQuery(id+"F4.wireOp",EDGE,"E60.1.46"),sQuery(id+"F4.wireOp",EDGE,"E60.2.0"),sQuery(id+"F4.wireOp",EDGE,"E60.2.1"),sQuery(id+"F4.wireOp",EDGE,"E60.2.2"),sQuery(id+"F4.wireOp",EDGE,"E60.2.4"),sQuery(id+"F4.wireOp",EDGE,"E60.2.5"),sQuery(id+"F4.wireOp",EDGE,"E60.2.6"),sQuery(id+"F4.wireOp",EDGE,"E60.2.7"),sQuery(id+"F4.wireOp",EDGE,"E60.2.11"),sQuery(id+"F4.wireOp",EDGE,"E60.2.13"),sQuery(id+"F4.wireOp",EDGE,"E60.2.15"),sQuery(id+"F4.wireOp",EDGE,"E60.2.16"),sQuery(id+"F4.wireOp",EDGE,"E60.2.18"),sQuery(id+"F4.wireOp",EDGE,"E60.2.21"),sQuery(id+"F4.wireOp",EDGE,"E60.2.22"),sQuery(id+"F4.wireOp",EDGE,"E60.2.23"),sQuery(id+"F4.wireOp",EDGE,"E60.2.25"),sQuery(id+"F4.wireOp",EDGE,"E60.2.27"),sQuery(id+"F4.wireOp",EDGE,"E60.2.28"),sQuery(id+"F4.wireOp",EDGE,"E60.2.29"),sQuery(id+"F4.wireOp",EDGE,"E60.2.30"),sQuery(id+"F4.wireOp",EDGE,"E60.2.31"),sQuery(id+"F4.wireOp",EDGE,"E60.2.32"),sQuery(id+"F4.wireOp",EDGE,"E60.2.33"),sQuery(id+"F4.wireOp",EDGE,"E60.2.34"),sQuery(id+"F4.wireOp",EDGE,"E60.2.35"),sQuery(id+"F4.wireOp",EDGE,"E60.2.36"),sQuery(id+"F4.wireOp",EDGE,"E60.2.37"),sQuery(id+"F4.wireOp",EDGE,"E60.2.38"),sQuery(id+"F4.wireOp",EDGE,"E60.2.39"),sQuery(id+"F4.wireOp",EDGE,"E60.2.40"),sQuery(id+"F4.wireOp",EDGE,"E60.2.41"),sQuery(id+"F4.wireOp",EDGE,"E60.2.42"),sQuery(id+"F4.wireOp",EDGE,"E60.2.43"),sQuery(id+"F4.wireOp",EDGE,"E60.2.44"),sQuery(id+"F4.wireOp",EDGE,"E60.2.45"),sQuery(id+"F4.wireOp",EDGE,"E60.2.46"),sQuery(id+"F4.wireOp",EDGE,"E60.3.0"),sQuery(id+"F4.wireOp",EDGE,"E60.3.1"),sQuery(id+"F4.wireOp",EDGE,"E60.3.2"),sQuery(id+"F4.wireOp",EDGE,"E60.3.4"),sQuery(id+"F4.wireOp",EDGE,"E60.3.5"),sQuery(id+"F4.wireOp",EDGE,"E60.3.6"),sQuery(id+"F4.wireOp",EDGE,"E60.3.7"),sQuery(id+"F4.wireOp",EDGE,"E60.3.11"),sQuery(id+"F4.wireOp",EDGE,"E60.3.13"),sQuery(id+"F4.wireOp",EDGE,"E60.3.15"),sQuery(id+"F4.wireOp",EDGE,"E60.3.16"),sQuery(id+"F4.wireOp",EDGE,"E60.3.18"),sQuery(id+"F4.wireOp",EDGE,"E60.3.21"),sQuery(id+"F4.wireOp",EDGE,"E60.3.22"),sQuery(id+"F4.wireOp",EDGE,"E60.3.23"),sQuery(id+"F4.wireOp",EDGE,"E60.3.25"),sQuery(id+"F4.wireOp",EDGE,"E60.3.27"),sQuery(id+"F4.wireOp",EDGE,"E60.3.28"),sQuery(id+"F4.wireOp",EDGE,"E60.3.29"),sQuery(id+"F4.wireOp",EDGE,"E60.3.30"),sQuery(id+"F4.wireOp",EDGE,"E60.3.31"),sQuery(id+"F4.wireOp",EDGE,"E60.3.32"),sQuery(id+"F4.wireOp",EDGE,"E60.3.33"),sQuery(id+"F4.wireOp",EDGE,"E60.3.34"),sQuery(id+"F4.wireOp",EDGE,"E60.3.35"),sQuery(id+"F4.wireOp",EDGE,"E60.3.36"),sQuery(id+"F4.wireOp",EDGE,"E60.3.37"),sQuery(id+"F4.wireOp",EDGE,"E60.3.38"),sQuery(id+"F4.wireOp",EDGE,"E60.3.39"),sQuery(id+"F4.wireOp",EDGE,"E60.3.40"),sQuery(id+"F4.wireOp",EDGE,"E60.3.41"),sQuery(id+"F4.wireOp",EDGE,"E60.3.42"),sQuery(id+"F4.wireOp",EDGE,"E60.3.43"),sQuery(id+"F4.wireOp",EDGE,"E60.3.44"),sQuery(id+"F4.wireOp",EDGE,"E60.3.45"),sQuery(id+"F4.wireOp",EDGE,"E60.3.46"),sQuery(id+"F4.wireOp",EDGE,"E60.4.0"),sQuery(id+"F4.wireOp",EDGE,"E60.4.1"),sQuery(id+"F4.wireOp",EDGE,"E60.4.2"),sQuery(id+"F4.wireOp",EDGE,"E60.4.4"),sQuery(id+"F4.wireOp",EDGE,"E60.4.5"),sQuery(id+"F4.wireOp",EDGE,"E60.4.6"),sQuery(id+"F4.wireOp",EDGE,"E60.4.7"),sQuery(id+"F4.wireOp",EDGE,"E60.4.11"),sQuery(id+"F4.wireOp",EDGE,"E60.4.13"),sQuery(id+"F4.wireOp",EDGE,"E60.4.15"),sQuery(id+"F4.wireOp",EDGE,"E60.4.16"),sQuery(id+"F4.wireOp",EDGE,"E60.4.18"),sQuery(id+"F4.wireOp",EDGE,"E60.4.21"),sQuery(id+"F4.wireOp",EDGE,"E60.4.22"),sQuery(id+"F4.wireOp",EDGE,"E60.4.23"),sQuery(id+"F4.wireOp",EDGE,"E60.4.25"),sQuery(id+"F4.wireOp",EDGE,"E60.4.27"),sQuery(id+"F4.wireOp",EDGE,"E60.4.28"),sQuery(id+"F4.wireOp",EDGE,"E60.4.29"),sQuery(id+"F4.wireOp",EDGE,"E60.4.30"),sQuery(id+"F4.wireOp",EDGE,"E60.4.31"),sQuery(id+"F4.wireOp",EDGE,"E60.4.32"),sQuery(id+"F4.wireOp",EDGE,"E60.4.33"),sQuery(id+"F4.wireOp",EDGE,"E60.4.34"),sQuery(id+"F4.wireOp",EDGE,"E60.4.35"),sQuery(id+"F4.wireOp",EDGE,"E60.4.36"),sQuery(id+"F4.wireOp",EDGE,"E60.4.37"),sQuery(id+"F4.wireOp",EDGE,"E60.4.38"),sQuery(id+"F4.wireOp",EDGE,"E60.4.39"),sQuery(id+"F4.wireOp",EDGE,"E60.4.40"),sQuery(id+"F4.wireOp",EDGE,"E60.4.41"),sQuery(id+"F4.wireOp",EDGE,"E60.4.42"),sQuery(id+"F4.wireOp",EDGE,"E60.4.43"),sQuery(id+"F4.wireOp",EDGE,"E60.4.44"),sQuery(id+"F4.wireOp",EDGE,"E60.4.45"),sQuery(id+"F4.wireOp",EDGE,"E60.4.46"),sQuery(id+"F4.wireOp",EDGE,"E60.5.0"),sQuery(id+"F4.wireOp",EDGE,"E60.5.1"),sQuery(id+"F4.wireOp",EDGE,"E60.5.2"),sQuery(id+"F4.wireOp",EDGE,"E60.5.4"),sQuery(id+"F4.wireOp",EDGE,"E60.5.5"),sQuery(id+"F4.wireOp",EDGE,"E60.5.6"),sQuery(id+"F4.wireOp",EDGE,"E60.5.7"),sQuery(id+"F4.wireOp",EDGE,"E60.5.11"),sQuery(id+"F4.wireOp",EDGE,"E60.5.13"),sQuery(id+"F4.wireOp",EDGE,"E60.5.15"),sQuery(id+"F4.wireOp",EDGE,"E60.5.16"),sQuery(id+"F4.wireOp",EDGE,"E60.5.18"),sQuery(id+"F4.wireOp",EDGE,"E60.5.21"),sQuery(id+"F4.wireOp",EDGE,"E60.5.22"),sQuery(id+"F4.wireOp",EDGE,"E60.5.23"),sQuery(id+"F4.wireOp",EDGE,"E60.5.25"),sQuery(id+"F4.wireOp",EDGE,"E60.5.27"),sQuery(id+"F4.wireOp",EDGE,"E60.5.28"),sQuery(id+"F4.wireOp",EDGE,"E60.5.29"),sQuery(id+"F4.wireOp",EDGE,"E60.5.30"),sQuery(id+"F4.wireOp",EDGE,"E60.5.31"),sQuery(id+"F4.wireOp",EDGE,"E60.5.32"),sQuery(id+"F4.wireOp",EDGE,"E60.5.33"),sQuery(id+"F4.wireOp",EDGE,"E60.5.34"),sQuery(id+"F4.wireOp",EDGE,"E60.5.35"),sQuery(id+"F4.wireOp",EDGE,"E60.5.36"),sQuery(id+"F4.wireOp",EDGE,"E60.5.37"),sQuery(id+"F4.wireOp",EDGE,"E60.5.38"),sQuery(id+"F4.wireOp",EDGE,"E60.5.39"),sQuery(id+"F4.wireOp",EDGE,"E60.5.40"),sQuery(id+"F4.wireOp",EDGE,"E60.5.41"),sQuery(id+"F4.wireOp",EDGE,"E60.5.42"),sQuery(id+"F4.wireOp",EDGE,"E60.5.43"),sQuery(id+"F4.wireOp",EDGE,"E60.5.44"),sQuery(id+"F4.wireOp",EDGE,"E60.5.45"),sQuery(id+"F4.wireOp",EDGE,"E60.5.46"),sQuery(id+"F4.wireOp",EDGE,"E61"),sQuery(id+"F4.wireOp",EDGE,"E62"),sQuery(id+"F4.wireOp",EDGE,"E63"),sQuery(id+"F4.wireOp",EDGE,"E64"),sQuery(id+"F4.wireOp",EDGE,"E65"),sQuery(id+"F4.wireOp",EDGE,"E66")])]});
            var Q1;
            Q1=sQuery(id+"F7.wireOp",VERTEX,"E68.center");
            transform(context, id + "F11", {"entities" : qUnion([Q0]), "transformType" : TransformType.SCALE_UNIFORMLY, "scale" : 0.75, "scalePoint" : qUnion([Q1]), "makeCopy" : false});
        }
        {
            var Q0;
            {var subQ0=sQuery(id+"F7.wireOp",EDGE,"E71");var subQ1=sQuery(id+"F4.wireOp",EDGE,"E58.filletArc");Q0=makeQuery(id+"F9.boolean.opBoolean","MERGE",FACE,{"derivedFrom":[makeQuery(id+"F8.boolean.opBoolean","MERGE",FACE,{"derivedFrom":[makeQuery(id+"F6.boolean.opBoolean","COPY",FACE,{"derivedFrom":makeQuery(id+"F6.opExtrude","CAP_FACE",FACE,{"disambiguationData":[OSD([sQuery(id+"F0.wireOp",EDGE,"E0")])],"isStart":false})}),makeQuery(id+"F8.opExtrude","CAP_FACE",FACE,{"disambiguationData":[OSD([sQuery(id+"F4.wireOp",EDGE,"E20"),sQuery(id+"F4.wireOp",EDGE,"E41.MirrorCS"),subQ1,subQ0])],"isStart":false})]}),makeQuery(id+"F9.opExtrude","CAP_FACE",FACE,{"disambiguationData":[OSD([sQuery(id+"F4.wireOp",EDGE,"E21"),sQuery(id+"F4.wireOp",EDGE,"E42.MirrorCS"),subQ1,sQuery(id+"F4.wireOp",EDGE,"E59.filletArc"),sQuery(id+"F7.wireOp",EDGE,"E69"),subQ0])],"isStart":false}),makeQuery(id+"F9.opExtrude","CAP_FACE",FACE,{"disambiguationData":[OSD([sQuery(id+"F4.wireOp",EDGE,"E60.5.2"),sQuery(id+"F4.wireOp",EDGE,"E60.5.6"),sQuery(id+"F4.wireOp",EDGE,"E60.5.35"),sQuery(id+"F4.wireOp",EDGE,"E60.5.40"),sQuery(id+"F4.wireOp",EDGE,"E60.5.44"),sQuery(id+"F4.wireOp",EDGE,"E60.5.46"),sQuery(id+"F7.wireOp",EDGE,"E70.1.0"),sQuery(id+"F7.wireOp",EDGE,"E72.1.0")])],"isStart":false}),makeQuery(id+"F9.opExtrude","CAP_FACE",FACE,{"disambiguationData":[OSD([sQuery(id+"F4.wireOp",EDGE,"E60.4.2"),sQuery(id+"F4.wireOp",EDGE,"E60.4.6"),sQuery(id+"F4.wireOp",EDGE,"E60.4.40"),sQuery(id+"F4.wireOp",EDGE,"E60.4.46"),sQuery(id+"F7.wireOp",EDGE,"E70.2.0"),sQuery(id+"F7.wireOp",EDGE,"E72.2.0")])],"isStart":false}),makeQuery(id+"F9.opExtrude","CAP_FACE",FACE,{"disambiguationData":[OSD([sQuery(id+"F4.wireOp",EDGE,"E60.2.2"),sQuery(id+"F4.wireOp",EDGE,"E60.2.6"),sQuery(id+"F4.wireOp",EDGE,"E60.2.40"),sQuery(id+"F4.wireOp",EDGE,"E60.2.46"),sQuery(id+"F7.wireOp",EDGE,"E70.4.0"),sQuery(id+"F7.wireOp",EDGE,"E73.1.4.0")])],"isStart":false}),makeQuery(id+"F9.opExtrude","CAP_FACE",FACE,{"disambiguationData":[OSD([sQuery(id+"F4.wireOp",EDGE,"E60.1.2"),sQuery(id+"F4.wireOp",EDGE,"E60.1.6"),sQuery(id+"F4.wireOp",EDGE,"E60.1.35"),sQuery(id+"F4.wireOp",EDGE,"E60.1.40"),sQuery(id+"F4.wireOp",EDGE,"E60.1.44"),sQuery(id+"F4.wireOp",EDGE,"E60.1.46"),sQuery(id+"F7.wireOp",EDGE,"E70.5.0"),sQuery(id+"F7.wireOp",EDGE,"E73.1.5.0")])],"isStart":false})]});}
            extrude(context, id + "F12", {"entities" : qUnion([Q0]), "operationType" : NewBodyOperationType.ADD, "oppositeDirection" : true, "depth" : 5 * mm, "offsetDistance" : 25 * mm});
        }
        {
            var Q0;
            {var subQ0=sQuery(id+"F4.wireOp",EDGE,"E60.3.44");var subQ1=sQuery(id+"F4.wireOp",EDGE,"E60.3.35");Q0=makeQuery(id+"F12.boolean.opBoolean","MERGE",FACE,{"derivedFrom":[makeQuery(id+"F5.opExtrude","SWEPT_FACE",FACE,{"disambiguationData":[OSD([subQ1,subQ0])]}),makeQuery(id+"F12.opExtrude","SWEPT_FACE",FACE,{"disambiguationData":[OSD([sQuery(id+"F0.wireOp",EDGE,"E0"),subQ1,subQ0])]})]});}
            var sketch = newSketch(context, id + "F13", { "sketchPlane" : qUnion([Q0])});
            skLineSegment(sketch, "E74.bottom", {"start": v(-2.3, 25.32) * mm, "end": v(2.3, 25.32) * mm});
            skLineSegment(sketch, "E74.top", {"start": v(-2.3, 23.02) * mm, "end": v(2.3, 23.02) * mm});
            skLineSegment(sketch, "E74.left", {"start": v(-2.3, 25.32) * mm, "end": v(-2.3, 23.02) * mm});
            skLineSegment(sketch, "E74.right", {"start": v(2.3, 25.32) * mm, "end": v(2.3, 23.02) * mm});
            skLineSegment(sketch, "E75.bottom", {"start": v(-3.47, 30.32) * mm, "end": v(3.47, 30.32) * mm});
            skLineSegment(sketch, "E75.top", {"start": v(-3.47, 15.72) * mm, "end": v(3.47, 15.72) * mm});
            skLineSegment(sketch, "E75.left", {"start": v(-3.47, 30.32) * mm, "end": v(-3.47, 15.72) * mm});
            skLineSegment(sketch, "E75.right", {"start": v(3.47, 30.32) * mm, "end": v(3.47, 15.72) * mm});
            skPoint(sketch, "E75.middle", {"position": v(0, 23.02) * mm});
            skSolve(sketch);
        }
        {
            var Q0;
            Q0 = qSketchRegion(id + "F13", true);
            extrude(context, id + "F14", {"entities" : qUnion([Q0]), "operationType" : NewBodyOperationType.REMOVE, "oppositeDirection" : true, "depth" : 7 * mm, "offsetDistance" : 25 * mm, "hasSecondDirection" : true, "secondDirectionOppositeDirection" : false, "secondDirectionDepth" : 0 * mm});
        }
    });
